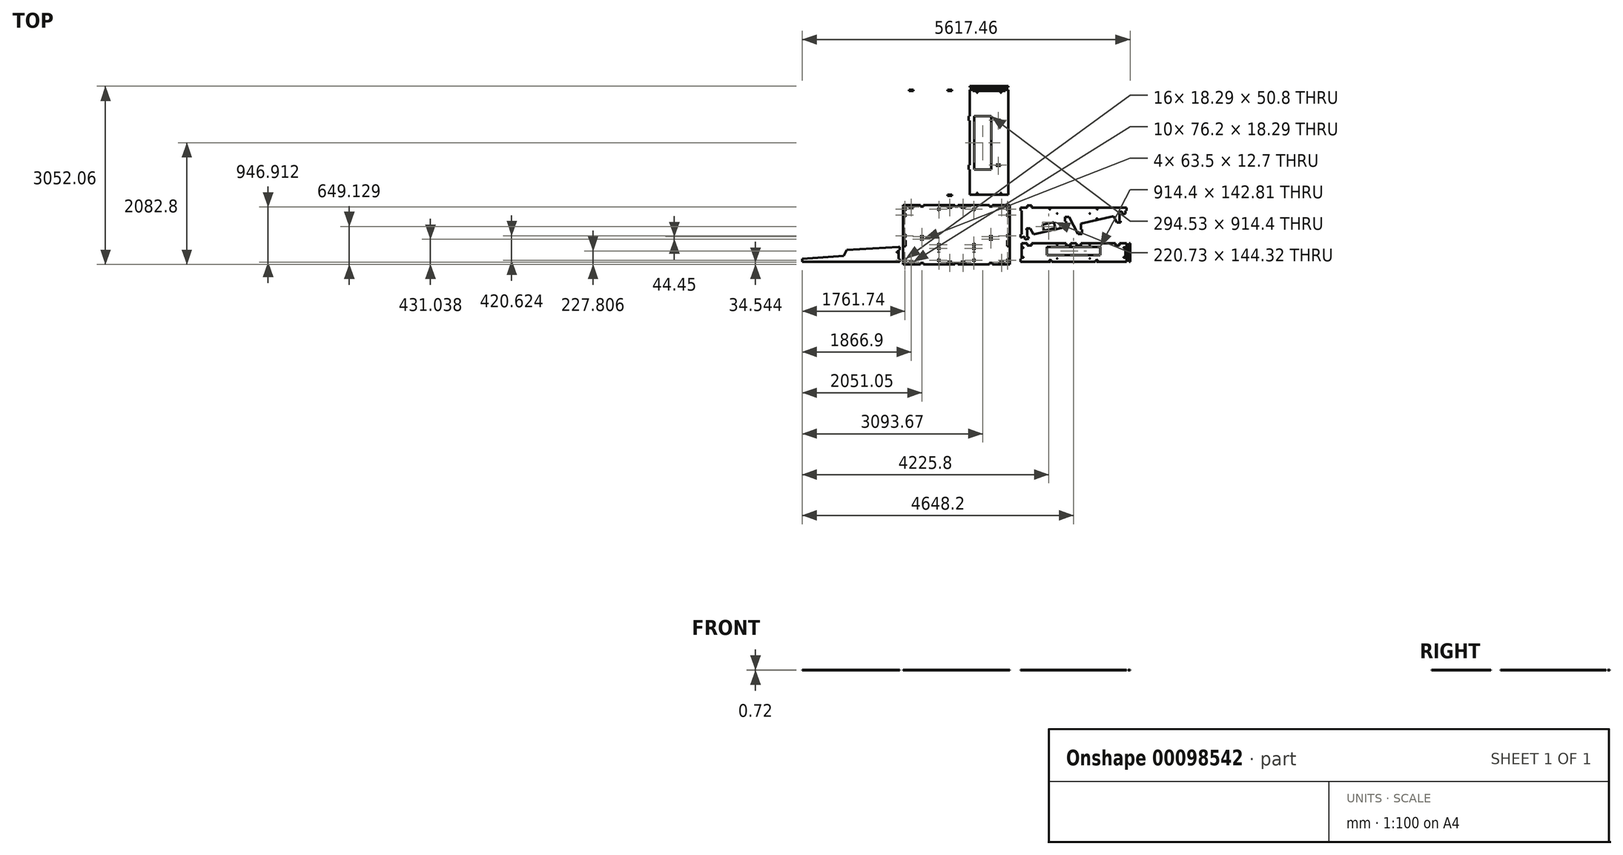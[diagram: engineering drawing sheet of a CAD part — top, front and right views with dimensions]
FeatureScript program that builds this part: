
annotation { "Feature Type Name" : "Feature", "Feature Type Description" : "" }
export const myFeature = defineFeature(function(context is Context, id is Id, definition is map)
    precondition{}
    {
        {
            assignVariable(context, id + "F0", {"name" : "ply34", "anyValue" : .72});
        }
        {
            var Q0;
            Q0=qCreatedBy(makeId("Top.planeOp"),FACE);
            var sketch = newSketch(context, id + "F1", { "sketchPlane" : qUnion([Q0])});
            skLineSegment(sketch, "E0.bottom", {"start": v(914.4, 508) * mm, "end": v(-914.4, 508) * mm});
            skLineSegment(sketch, "E0.top", {"start": v(914.4, -508) * mm, "end": v(-914.4, -508) * mm});
            skLineSegment(sketch, "E0.left", {"start": v(914.4, 508) * mm, "end": v(914.4, -508) * mm});
            skLineSegment(sketch, "E0.right", {"start": v(-914.4, 508) * mm, "end": v(-914.4, -508) * mm});
            skPoint(sketch, "E0.middle", {"position": v(0, 0) * mm});
            skLineSegment(sketch, "E1.bottom", {"start": v(889, 482.6) * mm, "end": v(-889, 482.6) * mm, "construction": true});
            skLineSegment(sketch, "E1.top", {"start": v(889, -482.6) * mm, "end": v(-889, -482.6) * mm, "construction": true});
            skLineSegment(sketch, "E1.left", {"start": v(889, 482.6) * mm, "end": v(889, -482.6) * mm, "construction": true});
            skLineSegment(sketch, "E1.right", {"start": v(-889, 482.6) * mm, "end": v(-889, -482.6) * mm, "construction": true});
            skLineSegment(sketch, "E2", {"start": v(0, 482.6) * mm, "end": v(0, -482.6) * mm, "construction": true});
            skLineSegment(sketch, "E3", {"start": v(0, 0) * mm, "end": v(-889, 0) * mm, "construction": true});
            skLineSegment(sketch, "E4", {"start": v(-444.5, 482.6) * mm, "end": v(-444.5, -482.6) * mm, "construction": true});
            skPoint(sketch, "E4.startSnap0", {"position": v(-444.5, 0) * mm});
            skLineSegment(sketch, "E5.bottom", {"start": v(-812.8, 482.6) * mm, "end": v(-736.6, 482.6) * mm});
            skLineSegment(sketch, "E5.top", {"start": v(-812.8, 464.31) * mm, "end": v(-736.6, 464.31) * mm});
            skLineSegment(sketch, "E5.left", {"start": v(-812.8, 482.6) * mm, "end": v(-812.8, 464.31) * mm});
            skLineSegment(sketch, "E5.right", {"start": v(-736.6, 482.6) * mm, "end": v(-736.6, 464.31) * mm});
            skLineSegment(sketch, "E6.MirrorCS", {"start": v(-76.2, 482.6) * mm, "end": v(-152.4, 482.6) * mm});
            skLineSegment(sketch, "E7.MirrorCS", {"start": v(-76.2, 464.31) * mm, "end": v(-152.4, 464.31) * mm});
            skLineSegment(sketch, "E8.MirrorCS", {"start": v(-152.4, 482.6) * mm, "end": v(-152.4, 464.31) * mm});
            skLineSegment(sketch, "E9.MirrorCS", {"start": v(-76.2, 482.6) * mm, "end": v(-76.2, 464.31) * mm});
            skLineSegment(sketch, "E10.MirrorCS", {"start": v(76.2, 482.6) * mm, "end": v(76.2, 464.31) * mm});
            skLineSegment(sketch, "E11.MirrorCS", {"start": v(736.6, 482.6) * mm, "end": v(736.6, 464.31) * mm});
            skLineSegment(sketch, "E12.MirrorCS", {"start": v(152.4, 482.6) * mm, "end": v(152.4, 464.31) * mm});
            skLineSegment(sketch, "E13.MirrorCS", {"start": v(812.8, 482.6) * mm, "end": v(812.8, 464.31) * mm});
            skLineSegment(sketch, "E14.MirrorCS", {"start": v(812.8, 482.6) * mm, "end": v(736.6, 482.6) * mm});
            skLineSegment(sketch, "E15.MirrorCS", {"start": v(76.2, 482.6) * mm, "end": v(152.4, 482.6) * mm});
            skLineSegment(sketch, "E16.MirrorCS", {"start": v(812.8, 464.31) * mm, "end": v(736.6, 464.31) * mm});
            skLineSegment(sketch, "E17.MirrorCS", {"start": v(76.2, 464.31) * mm, "end": v(152.4, 464.31) * mm});
            skLineSegment(sketch, "E18.MirrorCS", {"start": v(812.8, -482.6) * mm, "end": v(812.8, -464.31) * mm});
            skLineSegment(sketch, "E19.MirrorCS", {"start": v(-76.2, -482.6) * mm, "end": v(-76.2, -464.31) * mm});
            skLineSegment(sketch, "E20.MirrorCS", {"start": v(736.6, -482.6) * mm, "end": v(736.6, -464.31) * mm});
            skLineSegment(sketch, "E21.MirrorCS", {"start": v(-152.4, -482.6) * mm, "end": v(-152.4, -464.31) * mm});
            skLineSegment(sketch, "E22.MirrorCS", {"start": v(152.4, -482.6) * mm, "end": v(152.4, -464.31) * mm});
            skLineSegment(sketch, "E23.MirrorCS", {"start": v(-812.8, -482.6) * mm, "end": v(-812.8, -464.31) * mm});
            skLineSegment(sketch, "E24.MirrorCS", {"start": v(76.2, -482.6) * mm, "end": v(76.2, -464.31) * mm});
            skLineSegment(sketch, "E25.MirrorCS", {"start": v(-736.6, -482.6) * mm, "end": v(-736.6, -464.31) * mm});
            skLineSegment(sketch, "E26.MirrorCS", {"start": v(76.2, -482.6) * mm, "end": v(152.4, -482.6) * mm});
            skLineSegment(sketch, "E27.MirrorCS", {"start": v(812.8, -464.31) * mm, "end": v(736.6, -464.31) * mm});
            skLineSegment(sketch, "E28.MirrorCS", {"start": v(812.8, -482.6) * mm, "end": v(736.6, -482.6) * mm});
            skLineSegment(sketch, "E29.MirrorCS", {"start": v(-76.2, -464.31) * mm, "end": v(-152.4, -464.31) * mm});
            skLineSegment(sketch, "E30.MirrorCS", {"start": v(-76.2, -482.6) * mm, "end": v(-152.4, -482.6) * mm});
            skLineSegment(sketch, "E31.MirrorCS", {"start": v(76.2, -464.31) * mm, "end": v(152.4, -464.31) * mm});
            skLineSegment(sketch, "E32.MirrorCS", {"start": v(-812.8, -464.31) * mm, "end": v(-736.6, -464.31) * mm});
            skLineSegment(sketch, "E33.MirrorCS", {"start": v(-812.8, -482.6) * mm, "end": v(-736.6, -482.6) * mm});
            skLineSegment(sketch, "E34.bottom", {"start": v(292.1, 464.31) * mm, "end": v(310.39, 464.31) * mm});
            skLineSegment(sketch, "E34.top", {"start": v(292.1, 413.51) * mm, "end": v(310.39, 413.51) * mm});
            skLineSegment(sketch, "E34.left", {"start": v(292.1, 464.31) * mm, "end": v(292.1, 413.51) * mm});
            skLineSegment(sketch, "E34.right", {"start": v(310.39, 464.31) * mm, "end": v(310.39, 413.51) * mm});
            skLineSegment(sketch, "E35.bottom", {"start": v(292.1, -145.29) * mm, "end": v(310.39, -145.29) * mm});
            skLineSegment(sketch, "E35.top", {"start": v(292.1, -196.09) * mm, "end": v(310.39, -196.09) * mm});
            skLineSegment(sketch, "E35.left", {"start": v(292.1, -145.29) * mm, "end": v(292.1, -196.09) * mm});
            skLineSegment(sketch, "E35.right", {"start": v(310.39, -145.29) * mm, "end": v(310.39, -196.09) * mm});
            skLineSegment(sketch, "E36.MirrorCS", {"start": v(-292.1, -196.09) * mm, "end": v(-310.39, -196.09) * mm});
            skLineSegment(sketch, "E37.MirrorCS", {"start": v(-292.1, -145.29) * mm, "end": v(-310.39, -145.29) * mm});
            skLineSegment(sketch, "E38.MirrorCS", {"start": v(-292.1, 413.51) * mm, "end": v(-310.39, 413.51) * mm});
            skLineSegment(sketch, "E39.MirrorCS", {"start": v(-292.1, 464.31) * mm, "end": v(-310.39, 464.31) * mm});
            skLineSegment(sketch, "E40.MirrorCS", {"start": v(-292.1, -145.29) * mm, "end": v(-292.1, -196.09) * mm});
            skLineSegment(sketch, "E41.MirrorCS", {"start": v(-310.39, 464.31) * mm, "end": v(-310.39, 413.51) * mm});
            skLineSegment(sketch, "E42.MirrorCS", {"start": v(-310.39, -145.29) * mm, "end": v(-310.39, -196.09) * mm});
            skLineSegment(sketch, "E43.MirrorCS", {"start": v(-292.1, 464.31) * mm, "end": v(-292.1, 413.51) * mm});
            skLineSegment(sketch, "E44.bottom", {"start": v(-889, 685.8) * mm, "end": v(0, 685.8) * mm});
            skLineSegment(sketch, "E44.top", {"start": v(-889, 2463.8) * mm, "end": v(0, 2463.8) * mm});
            skLineSegment(sketch, "E44.left", {"start": v(-889, 685.8) * mm, "end": v(-889, 2463.8) * mm});
            skLineSegment(sketch, "E44.right", {"start": v(0, 685.8) * mm, "end": v(0, 2463.8) * mm});
            skLineSegment(sketch, "E45.bottom", {"start": v(-812.8, 685.8) * mm, "end": v(-736.6, 685.8) * mm});
            skLineSegment(sketch, "E45.top", {"start": v(-812.8, 667.51) * mm, "end": v(-736.6, 667.51) * mm});
            skLineSegment(sketch, "E45.left", {"start": v(-812.8, 685.8) * mm, "end": v(-812.8, 667.51) * mm});
            skLineSegment(sketch, "E45.right", {"start": v(-736.6, 685.8) * mm, "end": v(-736.6, 667.51) * mm});
            skLineSegment(sketch, "E46", {"start": v(-444.5, 685.8) * mm, "end": v(-444.5, 2463.8) * mm, "construction": true});
            skLineSegment(sketch, "E47", {"start": v(0, 1574.8) * mm, "end": v(-889, 1574.8) * mm, "construction": true});
            skLineSegment(sketch, "E48.MirrorCS", {"start": v(-76.2, 667.51) * mm, "end": v(-152.4, 667.51) * mm});
            skLineSegment(sketch, "E49.MirrorCS", {"start": v(-76.2, 685.8) * mm, "end": v(-152.4, 685.8) * mm});
            skLineSegment(sketch, "E50.MirrorCS", {"start": v(-152.4, 685.8) * mm, "end": v(-152.4, 667.51) * mm});
            skLineSegment(sketch, "E51.MirrorCS", {"start": v(-76.2, 685.8) * mm, "end": v(-76.2, 667.51) * mm});
            skLineSegment(sketch, "E52.MirrorCS", {"start": v(-812.8, 2482.09) * mm, "end": v(-736.6, 2482.09) * mm});
            skLineSegment(sketch, "E53.MirrorCS", {"start": v(-812.8, 2463.8) * mm, "end": v(-736.6, 2463.8) * mm});
            skLineSegment(sketch, "E54.MirrorCS", {"start": v(-812.8, 2463.8) * mm, "end": v(-812.8, 2482.09) * mm});
            skLineSegment(sketch, "E55.MirrorCS", {"start": v(-736.6, 2463.8) * mm, "end": v(-736.6, 2482.09) * mm});
            skLineSegment(sketch, "E56.MirrorCS", {"start": v(-152.4, 2463.8) * mm, "end": v(-152.4, 2482.09) * mm});
            skLineSegment(sketch, "E57.MirrorCS", {"start": v(-76.2, 2463.8) * mm, "end": v(-76.2, 2482.09) * mm});
            skLineSegment(sketch, "E58.MirrorCS", {"start": v(-76.2, 2482.09) * mm, "end": v(-152.4, 2482.09) * mm});
            skLineSegment(sketch, "E59.MirrorCS", {"start": v(-76.2, 2463.8) * mm, "end": v(-152.4, 2463.8) * mm});
            skLineSegment(sketch, "E60.0", {"start": v(870.71, 464.31) * mm, "end": v(-870.71, 464.31) * mm, "construction": true});
            skLineSegment(sketch, "E60.1", {"start": v(870.71, 464.31) * mm, "end": v(870.71, -464.31) * mm, "construction": true});
            skLineSegment(sketch, "E60.2", {"start": v(870.71, -464.31) * mm, "end": v(-870.71, -464.31) * mm, "construction": true});
            skLineSegment(sketch, "E60.3", {"start": v(-870.71, 464.31) * mm, "end": v(-870.71, -464.31) * mm, "construction": true});
            skLineSegment(sketch, "E61.bottom", {"start": v(-310.39, 464.31) * mm, "end": v(-292.1, 464.31) * mm, "construction": true});
            skLineSegment(sketch, "E61.top", {"start": v(-310.39, -196.09) * mm, "end": v(-292.1, -196.09) * mm, "construction": true});
            skLineSegment(sketch, "E61.left", {"start": v(-310.39, 464.31) * mm, "end": v(-310.39, -196.09) * mm, "construction": true});
            skLineSegment(sketch, "E61.right", {"start": v(-292.1, 464.31) * mm, "end": v(-292.1, -196.09) * mm, "construction": true});
            skLineSegment(sketch, "E62.bottom", {"start": v(292.1, 464.31) * mm, "end": v(310.39, 464.31) * mm, "construction": true});
            skLineSegment(sketch, "E62.top", {"start": v(292.1, -196.09) * mm, "end": v(310.39, -196.09) * mm, "construction": true});
            skLineSegment(sketch, "E62.left", {"start": v(292.1, 464.31) * mm, "end": v(292.1, -196.09) * mm, "construction": true});
            skLineSegment(sketch, "E62.right", {"start": v(310.39, 464.31) * mm, "end": v(310.39, -196.09) * mm, "construction": true});
            skLineSegment(sketch, "E63.bottom", {"start": v(228.6, 685.8) * mm, "end": v(889, 685.8) * mm});
            skLineSegment(sketch, "E63.top", {"start": v(228.6, 2463.8) * mm, "end": v(889, 2463.8) * mm});
            skLineSegment(sketch, "E63.left", {"start": v(228.6, 685.8) * mm, "end": v(228.6, 2463.8) * mm});
            skLineSegment(sketch, "E63.right", {"start": v(889, 685.8) * mm, "end": v(889, 2463.8) * mm});
            skLineSegment(sketch, "E64.bottom", {"start": v(228.6, 685.8) * mm, "end": v(279.4, 685.8) * mm});
            skLineSegment(sketch, "E64.top", {"start": v(228.6, 667.51) * mm, "end": v(279.4, 667.51) * mm});
            skLineSegment(sketch, "E64.left", {"start": v(228.6, 685.8) * mm, "end": v(228.6, 667.51) * mm});
            skLineSegment(sketch, "E64.right", {"start": v(279.4, 685.8) * mm, "end": v(279.4, 667.51) * mm});
            skLineSegment(sketch, "E65", {"start": v(558.8, 685.8) * mm, "end": v(558.8, 2463.8) * mm, "construction": true});
            skLineSegment(sketch, "E66", {"start": v(889, 1574.8) * mm, "end": v(228.6, 1574.8) * mm, "construction": true});
            skLineSegment(sketch, "E67.MirrorCS", {"start": v(889, 685.8) * mm, "end": v(838.2, 685.8) * mm});
            skLineSegment(sketch, "E68.MirrorCS", {"start": v(838.2, 685.8) * mm, "end": v(838.2, 667.51) * mm});
            skLineSegment(sketch, "E69.MirrorCS", {"start": v(889, 667.51) * mm, "end": v(838.2, 667.51) * mm});
            skLineSegment(sketch, "E70.MirrorCS", {"start": v(889, 685.8) * mm, "end": v(889, 667.51) * mm});
            skLineSegment(sketch, "E71.MirrorCS", {"start": v(889, 2463.8) * mm, "end": v(889, 2482.09) * mm});
            skLineSegment(sketch, "E72.MirrorCS", {"start": v(889, 2482.09) * mm, "end": v(838.2, 2482.09) * mm});
            skLineSegment(sketch, "E73.MirrorCS", {"start": v(838.2, 2463.8) * mm, "end": v(838.2, 2482.09) * mm});
            skLineSegment(sketch, "E74.MirrorCS", {"start": v(889, 2463.8) * mm, "end": v(838.2, 2463.8) * mm});
            skLineSegment(sketch, "E75.MirrorCS", {"start": v(228.6, 2463.8) * mm, "end": v(228.6, 2482.09) * mm});
            skLineSegment(sketch, "E76.MirrorCS", {"start": v(228.6, 2463.8) * mm, "end": v(279.4, 2463.8) * mm});
            skLineSegment(sketch, "E77.MirrorCS", {"start": v(279.4, 2463.8) * mm, "end": v(279.4, 2482.09) * mm});
            skLineSegment(sketch, "E78.MirrorCS", {"start": v(228.6, 2482.09) * mm, "end": v(279.4, 2482.09) * mm});
            skPoint(sketch, "E79.middle", {"position": v(558.8, 1574.8) * mm});
            skLineSegment(sketch, "E80.bottom", {"start": v(304.8, 2032) * mm, "end": v(599.33, 2032) * mm});
            skLineSegment(sketch, "E80.top", {"start": v(304.8, 1117.6) * mm, "end": v(599.33, 1117.6) * mm});
            skLineSegment(sketch, "E80.left", {"start": v(304.8, 2032) * mm, "end": v(304.8, 1117.6) * mm});
            skLineSegment(sketch, "E80.right", {"start": v(599.33, 2032) * mm, "end": v(599.33, 1117.6) * mm});
            skLineSegment(sketch, "E81", {"start": v(304.8, 1574.8) * mm, "end": v(599.33, 1574.8) * mm});
            skLineSegment(sketch, "E82.bottom", {"start": v(1117.6, 464.31) * mm, "end": v(2895.6, 464.31) * mm, "construction": true});
            skLineSegment(sketch, "E82.top", {"start": v(1117.6, -145.29) * mm, "end": v(2895.6, -145.29) * mm, "construction": true});
            skLineSegment(sketch, "E82.left", {"start": v(1117.6, 464.31) * mm, "end": v(1117.6, -145.29) * mm, "construction": true});
            skLineSegment(sketch, "E82.right", {"start": v(2895.6, 464.31) * mm, "end": v(2895.6, -145.29) * mm, "construction": true});
            skLineSegment(sketch, "E83", {"start": v(2133.6, 464.31) * mm, "end": v(2133.6, -145.29) * mm, "construction": true});
            skLineSegment(sketch, "E84", {"start": v(1117.6, -43.69) * mm, "end": v(2895.6, -43.69) * mm, "construction": true});
            skLineSegment(sketch, "E85", {"start": v(1117.6, 362.71) * mm, "end": v(2895.6, 362.71) * mm, "construction": true});
            skLineSegment(sketch, "E86", {"start": v(1117.6, 464.31) * mm, "end": v(2895.6, 464.31) * mm});
            skLineSegment(sketch, "E87", {"start": v(2895.6, 464.31) * mm, "end": v(2895.6, 362.71) * mm});
            skLineSegment(sketch, "E88", {"start": v(2895.6, 362.71) * mm, "end": v(1117.6, -43.69) * mm});
            skLineSegment(sketch, "E89", {"start": v(1117.6, -43.69) * mm, "end": v(1117.6, 464.31) * mm});
            skLineSegment(sketch, "E90", {"start": v(2133.6, 188.54) * mm, "end": v(2133.6, 14.22) * mm});
            skLineSegment(sketch, "E91", {"start": v(2133.6, 14.22) * mm, "end": v(2082.8, 14.22) * mm});
            skLineSegment(sketch, "E92", {"start": v(2082.8, 14.22) * mm, "end": v(2006.6, 159.51) * mm});
            skLineSegment(sketch, "E93.bottom", {"start": v(2133.6, 464.31) * mm, "end": v(2057.4, 464.31) * mm});
            skLineSegment(sketch, "E93.top", {"start": v(2133.6, 500.89) * mm, "end": v(2057.4, 500.89) * mm});
            skLineSegment(sketch, "E93.left", {"start": v(2133.6, 464.31) * mm, "end": v(2133.6, 500.89) * mm});
            skLineSegment(sketch, "E93.right", {"start": v(2057.4, 464.31) * mm, "end": v(2057.4, 500.89) * mm});
            skLineSegment(sketch, "E94.bottom", {"start": v(2133.6, 14.22) * mm, "end": v(2151.89, 14.22) * mm});
            skLineSegment(sketch, "E94.top", {"start": v(2133.6, 90.42) * mm, "end": v(2151.89, 90.42) * mm});
            skLineSegment(sketch, "E94.left", {"start": v(2133.6, 14.22) * mm, "end": v(2133.6, 90.42) * mm});
            skLineSegment(sketch, "E94.right", {"start": v(2151.89, 14.22) * mm, "end": v(2151.89, 90.42) * mm});
            skLineSegment(sketch, "E95", {"start": v(1879.6, 464.31) * mm, "end": v(1879.6, -145.29) * mm, "construction": true});
            skLineSegment(sketch, "E96.bottom", {"start": v(1879.6, 304.8) * mm, "end": v(1861.31, 304.8) * mm});
            skLineSegment(sketch, "E96.top", {"start": v(1879.6, 228.6) * mm, "end": v(1861.31, 228.6) * mm});
            skLineSegment(sketch, "E96.left", {"start": v(1879.6, 304.8) * mm, "end": v(1879.6, 228.6) * mm});
            skLineSegment(sketch, "E96.right", {"start": v(1861.31, 304.8) * mm, "end": v(1861.31, 228.6) * mm});
            skLineSegment(sketch, "E97", {"start": v(1879.6, 304.8) * mm, "end": v(1930.4, 304.8) * mm});
            skLineSegment(sketch, "E98", {"start": v(1879.6, 228.6) * mm, "end": v(1879.6, 130.48) * mm});
            skLineSegment(sketch, "E99.bottom", {"start": v(1879.6, -145.29) * mm, "end": v(1955.8, -145.29) * mm});
            skLineSegment(sketch, "E99.top", {"start": v(1879.6, -181.86) * mm, "end": v(1955.8, -181.86) * mm});
            skLineSegment(sketch, "E99.left", {"start": v(1879.6, -145.29) * mm, "end": v(1879.6, -181.86) * mm});
            skLineSegment(sketch, "E99.right", {"start": v(1955.8, -145.29) * mm, "end": v(1955.8, -181.86) * mm});
            skLineSegment(sketch, "E100", {"start": v(1117.6, -43.69) * mm, "end": v(1117.6, -145.29) * mm});
            skLineSegment(sketch, "E101", {"start": v(2895.6, -145.29) * mm, "end": v(1117.6, -145.29) * mm});
            skLineSegment(sketch, "E102", {"start": v(2895.6, -145.29) * mm, "end": v(2895.6, 362.71) * mm});
            skLineSegment(sketch, "E103", {"start": v(2006.6, 159.51) * mm, "end": v(1930.4, 304.8) * mm});
            skLineSegment(sketch, "E104.0", {"start": v(678.69, 2032) * mm, "end": v(678.69, 1117.6) * mm, "construction": true});
            skLineSegment(sketch, "E105.bottom", {"start": v(678.69, 1181.1) * mm, "end": v(754.89, 1181.1) * mm});
            skLineSegment(sketch, "E105.top", {"start": v(678.69, 1199.39) * mm, "end": v(754.89, 1199.39) * mm});
            skLineSegment(sketch, "E105.left", {"start": v(678.69, 1181.1) * mm, "end": v(678.69, 1199.39) * mm});
            skLineSegment(sketch, "E105.right", {"start": v(754.89, 1181.1) * mm, "end": v(754.89, 1199.39) * mm});
            skLineSegment(sketch, "E106.MirrorCS", {"start": v(754.89, 1968.5) * mm, "end": v(754.89, 1950.21) * mm});
            skLineSegment(sketch, "E107.MirrorCS", {"start": v(678.69, 1950.21) * mm, "end": v(754.89, 1950.21) * mm});
            skLineSegment(sketch, "E108.MirrorCS", {"start": v(678.69, 1968.5) * mm, "end": v(754.89, 1968.5) * mm});
            skLineSegment(sketch, "E109.MirrorCS", {"start": v(678.69, 1968.5) * mm, "end": v(678.69, 1950.21) * mm});
            skLineSegment(sketch, "E110.bottom", {"start": v(1117.6, 464.31) * mm, "end": v(1099.31, 464.31) * mm});
            skLineSegment(sketch, "E110.top", {"start": v(1117.6, 413.51) * mm, "end": v(1099.31, 413.51) * mm});
            skLineSegment(sketch, "E110.left", {"start": v(1117.6, 464.31) * mm, "end": v(1117.6, 413.51) * mm});
            skLineSegment(sketch, "E110.right", {"start": v(1099.31, 464.31) * mm, "end": v(1099.31, 413.51) * mm});
            skLineSegment(sketch, "E111.bottom", {"start": v(1117.6, -43.69) * mm, "end": v(1099.31, -43.69) * mm});
            skLineSegment(sketch, "E111.top", {"start": v(1117.6, 7.11) * mm, "end": v(1099.31, 7.11) * mm});
            skLineSegment(sketch, "E111.left", {"start": v(1117.6, -43.69) * mm, "end": v(1117.6, 7.11) * mm});
            skLineSegment(sketch, "E111.right", {"start": v(1099.31, -43.69) * mm, "end": v(1099.31, 7.11) * mm});
            skLineSegment(sketch, "E112.bottom", {"start": v(889, 464.31) * mm, "end": v(870.71, 464.31) * mm});
            skLineSegment(sketch, "E112.top", {"start": v(889, 413.51) * mm, "end": v(870.71, 413.51) * mm});
            skLineSegment(sketch, "E112.left", {"start": v(889, 464.31) * mm, "end": v(889, 413.51) * mm});
            skLineSegment(sketch, "E112.right", {"start": v(870.71, 464.31) * mm, "end": v(870.71, 413.51) * mm});
            skLineSegment(sketch, "E113.bottom", {"start": v(1099.31, -94.49) * mm, "end": v(1117.6, -94.49) * mm});
            skLineSegment(sketch, "E113.top", {"start": v(1099.31, -145.29) * mm, "end": v(1117.6, -145.29) * mm});
            skLineSegment(sketch, "E113.left", {"start": v(1099.31, -94.49) * mm, "end": v(1099.31, -145.29) * mm});
            skLineSegment(sketch, "E113.right", {"start": v(1117.6, -94.49) * mm, "end": v(1117.6, -145.29) * mm});
            skLineSegment(sketch, "E114.bottom", {"start": v(889, -94.49) * mm, "end": v(870.71, -94.49) * mm});
            skLineSegment(sketch, "E114.top", {"start": v(889, -145.29) * mm, "end": v(870.71, -145.29) * mm});
            skLineSegment(sketch, "E114.left", {"start": v(889, -94.49) * mm, "end": v(889, -145.29) * mm});
            skLineSegment(sketch, "E114.right", {"start": v(870.71, -94.49) * mm, "end": v(870.71, -145.29) * mm});
            skLineSegment(sketch, "E115.MirrorCS", {"start": v(-889, 464.31) * mm, "end": v(-870.71, 464.31) * mm});
            skLineSegment(sketch, "E116.MirrorCS", {"start": v(-889, -145.29) * mm, "end": v(-870.71, -145.29) * mm});
            skLineSegment(sketch, "E117.MirrorCS", {"start": v(-889, -94.49) * mm, "end": v(-870.71, -94.49) * mm});
            skLineSegment(sketch, "E118.MirrorCS", {"start": v(-889, 413.51) * mm, "end": v(-870.71, 413.51) * mm});
            skLineSegment(sketch, "E119.MirrorCS", {"start": v(-870.71, -94.49) * mm, "end": v(-870.71, -145.29) * mm});
            skLineSegment(sketch, "E120.MirrorCS", {"start": v(-889, -94.49) * mm, "end": v(-889, -145.29) * mm});
            skLineSegment(sketch, "E121.MirrorCS", {"start": v(-870.71, 464.31) * mm, "end": v(-870.71, 413.51) * mm});
            skLineSegment(sketch, "E122.MirrorCS", {"start": v(-889, 464.31) * mm, "end": v(-889, 413.51) * mm});
            skLineSegment(sketch, "E123", {"start": v(-50.8, 2463.8) * mm, "end": v(-50.8, 685.8) * mm, "construction": true});
            skLineSegment(sketch, "E124.bottom", {"start": v(889, 7.11) * mm, "end": v(870.71, 7.11) * mm});
            skLineSegment(sketch, "E124.top", {"start": v(889, -43.69) * mm, "end": v(870.71, -43.69) * mm});
            skLineSegment(sketch, "E124.left", {"start": v(889, 7.11) * mm, "end": v(889, -43.69) * mm});
            skLineSegment(sketch, "E124.right", {"start": v(870.71, 7.11) * mm, "end": v(870.71, -43.69) * mm});
            skLineSegment(sketch, "E125.MirrorCS", {"start": v(-870.71, 7.11) * mm, "end": v(-870.71, -43.69) * mm});
            skLineSegment(sketch, "E126.MirrorCS", {"start": v(-889, 7.11) * mm, "end": v(-889, -43.69) * mm});
            skLineSegment(sketch, "E127.MirrorCS", {"start": v(-889, -43.69) * mm, "end": v(-870.71, -43.69) * mm});
            skLineSegment(sketch, "E128.MirrorCS", {"start": v(-889, 7.11) * mm, "end": v(-870.71, 7.11) * mm});
            skLineSegment(sketch, "E129.MirrorCS", {"start": v(-838.2, 2463.8) * mm, "end": v(-838.2, 685.8) * mm, "construction": true});
            skLineSegment(sketch, "E130.0", {"start": v(1117.6, 482.6) * mm, "end": v(2895.6, 482.6) * mm, "construction": true});
            skLineSegment(sketch, "E131", {"start": v(1203.45, -24.06) * mm, "end": v(2936.75, 372.12) * mm, "construction": true});
            skLineSegment(sketch, "E132", {"start": v(2936.75, 372.12) * mm, "end": v(2940.82, 354.29) * mm, "construction": true});
            skLineSegment(sketch, "E133", {"start": v(2940.82, 354.29) * mm, "end": v(1207.53, -41.9) * mm, "construction": true});
            skLineSegment(sketch, "E134", {"start": v(1207.53, -41.9) * mm, "end": v(1203.45, -24.06) * mm, "construction": true});
            skLineSegment(sketch, "E135", {"start": v(2006.6, 159.51) * mm, "end": v(2133.6, 188.54) * mm, "construction": true});
            skPoint(sketch, "E136", {"position": v(2070.1, 174.03) * mm});
            skLineSegment(sketch, "E137.bottom", {"start": v(-50.8, 1676.4) * mm, "end": v(-69.09, 1676.4) * mm});
            skLineSegment(sketch, "E137.top", {"start": v(-50.8, 1473.2) * mm, "end": v(-69.09, 1473.2) * mm});
            skLineSegment(sketch, "E137.left", {"start": v(-50.8, 1676.4) * mm, "end": v(-50.8, 1473.2) * mm});
            skLineSegment(sketch, "E137.right", {"start": v(-69.09, 1676.4) * mm, "end": v(-69.09, 1473.2) * mm});
            skPoint(sketch, "E137.middle", {"position": v(-59.94, 1574.8) * mm});
            skLineSegment(sketch, "E138.bottom", {"start": v(-838.2, 685.8) * mm, "end": v(-819.91, 685.8) * mm});
            skLineSegment(sketch, "E138.top", {"start": v(-838.2, 698.5) * mm, "end": v(-819.91, 698.5) * mm});
            skLineSegment(sketch, "E138.left", {"start": v(-838.2, 685.8) * mm, "end": v(-838.2, 698.5) * mm});
            skLineSegment(sketch, "E138.right", {"start": v(-819.91, 685.8) * mm, "end": v(-819.91, 698.5) * mm});
            skLineSegment(sketch, "E139.MirrorCS", {"start": v(-69.09, 685.8) * mm, "end": v(-69.09, 698.5) * mm});
            skLineSegment(sketch, "E140.MirrorCS", {"start": v(-50.8, 685.8) * mm, "end": v(-50.8, 698.5) * mm});
            skLineSegment(sketch, "E141.MirrorCS", {"start": v(-50.8, 685.8) * mm, "end": v(-69.09, 685.8) * mm});
            skLineSegment(sketch, "E142.MirrorCS", {"start": v(-50.8, 698.5) * mm, "end": v(-69.09, 698.5) * mm});
            skLineSegment(sketch, "E143.MirrorCS", {"start": v(-69.09, 2463.8) * mm, "end": v(-69.09, 2451.1) * mm});
            skLineSegment(sketch, "E144.MirrorCS", {"start": v(-50.8, 2463.8) * mm, "end": v(-50.8, 2451.1) * mm});
            skLineSegment(sketch, "E145.MirrorCS", {"start": v(-50.8, 2463.8) * mm, "end": v(-69.09, 2463.8) * mm});
            skLineSegment(sketch, "E146.MirrorCS", {"start": v(-50.8, 2451.1) * mm, "end": v(-69.09, 2451.1) * mm});
            skLineSegment(sketch, "E147.MirrorCS", {"start": v(-838.2, 2463.8) * mm, "end": v(-819.91, 2463.8) * mm});
            skLineSegment(sketch, "E148.MirrorCS", {"start": v(-838.2, 2451.1) * mm, "end": v(-819.91, 2451.1) * mm});
            skLineSegment(sketch, "E149.MirrorCS", {"start": v(-819.91, 2463.8) * mm, "end": v(-819.91, 2451.1) * mm});
            skLineSegment(sketch, "E150.MirrorCS", {"start": v(-838.2, 2463.8) * mm, "end": v(-838.2, 2451.1) * mm});
            skLineSegment(sketch, "E151", {"start": v(1219.9, -39.06) * mm, "end": v(1215.83, -21.24) * mm});
            skLineSegment(sketch, "E152", {"start": v(1219.9, -39.06) * mm, "end": v(1232.29, -36.23) * mm});
            skLineSegment(sketch, "E153", {"start": v(1232.29, -36.23) * mm, "end": v(1239.36, -67.19) * mm});
            skLineSegment(sketch, "E154", {"start": v(1239.36, -67.19) * mm, "end": v(1177.46, -81.33) * mm});
            skLineSegment(sketch, "E155", {"start": v(1177.46, -81.33) * mm, "end": v(1166.3, -32.55) * mm});
            skLineSegment(sketch, "E156", {"start": v(1215.83, -21.24) * mm, "end": v(1215.83, 110.24) * mm});
            skLineSegment(sketch, "E157", {"start": v(1215.83, 110.24) * mm, "end": v(1266.63, 110.24) * mm});
            skLineSegment(sketch, "E158", {"start": v(1266.63, 110.24) * mm, "end": v(1322.77, 3.2) * mm});
            skLineSegment(sketch, "E159.bottom", {"start": v(1215.83, 110.24) * mm, "end": v(1197.54, 110.24) * mm});
            skLineSegment(sketch, "E159.top", {"start": v(1215.83, 84.84) * mm, "end": v(1197.54, 84.84) * mm});
            skLineSegment(sketch, "E159.left", {"start": v(1215.83, 110.24) * mm, "end": v(1215.83, 84.84) * mm});
            skLineSegment(sketch, "E159.right", {"start": v(1197.54, 110.24) * mm, "end": v(1197.54, 84.84) * mm});
            skLineSegment(sketch, "E160", {"start": v(2006.6, 159.51) * mm, "end": v(2059.14, -70.34) * mm, "construction": true});
            skLineSegment(sketch, "E161.MirrorCS", {"start": v(2801.44, 322.43) * mm, "end": v(2789.06, 319.6) * mm, "construction": true});
            skLineSegment(sketch, "E162.MirrorCS", {"start": v(2789.06, 319.6) * mm, "end": v(2796.14, 288.65) * mm, "construction": true});
            skLineSegment(sketch, "E163.MirrorCS", {"start": v(2813.82, 325.26) * mm, "end": v(2809.75, 343.09) * mm, "construction": true});
            skLineSegment(sketch, "E164.MirrorCS", {"start": v(2801.44, 322.43) * mm, "end": v(2797.37, 340.26) * mm, "construction": true});
            skLineSegment(sketch, "E165.MirrorCS", {"start": v(2740.25, 458.67) * mm, "end": v(2756.72, 466.62) * mm, "construction": true});
            skLineSegment(sketch, "E166.MirrorCS", {"start": v(2751.29, 435.8) * mm, "end": v(2767.76, 443.74) * mm, "construction": true});
            skLineSegment(sketch, "E167.MirrorCS", {"start": v(2796.14, 288.65) * mm, "end": v(2858.04, 302.8) * mm, "construction": true});
            skLineSegment(sketch, "E168.MirrorCS", {"start": v(2797.37, 340.26) * mm, "end": v(2740.25, 458.67) * mm, "construction": true});
            skLineSegment(sketch, "E169.MirrorCS", {"start": v(2858.04, 302.8) * mm, "end": v(2846.9, 351.58) * mm, "construction": true});
            skLineSegment(sketch, "E170.MirrorCS", {"start": v(2740.25, 458.67) * mm, "end": v(2694.5, 436.6) * mm, "construction": true});
            skLineSegment(sketch, "E171.MirrorCS", {"start": v(2694.5, 436.6) * mm, "end": v(2690.43, 315.82) * mm, "construction": true});
            skLineSegment(sketch, "E172.MirrorCS", {"start": v(2740.25, 458.67) * mm, "end": v(2751.29, 435.8) * mm, "construction": true});
            skLineSegment(sketch, "E173.MirrorCS", {"start": v(2756.72, 466.62) * mm, "end": v(2767.76, 443.74) * mm, "construction": true});
            skLineSegment(sketch, "E174.MirrorCS", {"start": v(2797.37, 234.19) * mm, "end": v(2815.66, 234.19) * mm});
            skLineSegment(sketch, "E175.MirrorCS", {"start": v(2793.3, 358.09) * mm, "end": v(2780.91, 355.26) * mm});
            skLineSegment(sketch, "E176.MirrorCS", {"start": v(2797.37, 208.79) * mm, "end": v(2815.66, 208.79) * mm});
            skLineSegment(sketch, "E177.MirrorCS", {"start": v(2793.3, 358.09) * mm, "end": v(2797.37, 340.26) * mm});
            skLineSegment(sketch, "E178.MirrorCS", {"start": v(2805.67, 360.92) * mm, "end": v(2809.75, 343.09) * mm, "construction": true});
            skLineSegment(sketch, "E179.MirrorCS", {"start": v(2797.37, 340.26) * mm, "end": v(2797.37, 208.79) * mm});
            skLineSegment(sketch, "E180.MirrorCS", {"start": v(2773.84, 386.2) * mm, "end": v(2835.74, 400.36) * mm});
            skLineSegment(sketch, "E181.MirrorCS", {"start": v(2780.91, 355.26) * mm, "end": v(2773.84, 386.2) * mm});
            skLineSegment(sketch, "E182.MirrorCS", {"start": v(2815.66, 208.79) * mm, "end": v(2815.66, 234.19) * mm});
            skLineSegment(sketch, "E183.MirrorCS", {"start": v(2797.37, 208.79) * mm, "end": v(2797.37, 234.19) * mm});
            skLineSegment(sketch, "E184.MirrorCS", {"start": v(2746.57, 208.79) * mm, "end": v(2690.43, 315.82) * mm});
            skLineSegment(sketch, "E185.MirrorCS", {"start": v(2797.37, 208.79) * mm, "end": v(2746.57, 208.79) * mm});
            skLineSegment(sketch, "E186.MirrorCS", {"start": v(2835.74, 400.36) * mm, "end": v(2846.9, 351.58) * mm});
            skLineSegment(sketch, "E187.bottom", {"start": v(1215.83, -145.29) * mm, "end": v(1292.03, -145.29) * mm});
            skLineSegment(sketch, "E187.top", {"start": v(1215.83, -181.86) * mm, "end": v(1292.03, -181.86) * mm});
            skLineSegment(sketch, "E187.left", {"start": v(1215.83, -145.29) * mm, "end": v(1215.83, -181.86) * mm});
            skLineSegment(sketch, "E187.right", {"start": v(1292.03, -145.29) * mm, "end": v(1292.03, -181.86) * mm});
            skLineSegment(sketch, "E188.bottom", {"start": v(2895.6, 464.31) * mm, "end": v(2913.89, 464.31) * mm});
            skLineSegment(sketch, "E188.top", {"start": v(2895.6, 413.51) * mm, "end": v(2913.89, 413.51) * mm});
            skLineSegment(sketch, "E188.left", {"start": v(2895.6, 464.31) * mm, "end": v(2895.6, 413.51) * mm});
            skLineSegment(sketch, "E188.right", {"start": v(2913.89, 464.31) * mm, "end": v(2913.89, 413.51) * mm});
            skLineSegment(sketch, "E189.bottom", {"start": v(2797.37, 464.31) * mm, "end": v(2721.17, 464.31) * mm});
            skLineSegment(sketch, "E189.top", {"start": v(2797.37, 500.89) * mm, "end": v(2721.17, 500.89) * mm});
            skLineSegment(sketch, "E189.left", {"start": v(2797.37, 464.31) * mm, "end": v(2797.37, 500.89) * mm});
            skLineSegment(sketch, "E189.right", {"start": v(2721.17, 464.31) * mm, "end": v(2721.17, 500.89) * mm});
            skLineSegment(sketch, "E190.bottom", {"start": v(2895.6, 362.71) * mm, "end": v(2913.89, 362.71) * mm});
            skLineSegment(sketch, "E190.top", {"start": v(2895.6, 311.91) * mm, "end": v(2913.89, 311.91) * mm});
            skLineSegment(sketch, "E190.left", {"start": v(2895.6, 362.71) * mm, "end": v(2895.6, 311.91) * mm});
            skLineSegment(sketch, "E190.right", {"start": v(2913.89, 362.71) * mm, "end": v(2913.89, 311.91) * mm});
            skLineSegment(sketch, "E191.bottom", {"start": v(2895.6, -145.29) * mm, "end": v(2913.89, -145.29) * mm});
            skLineSegment(sketch, "E191.top", {"start": v(2895.6, -94.49) * mm, "end": v(2913.89, -94.49) * mm});
            skLineSegment(sketch, "E191.left", {"start": v(2895.6, -145.29) * mm, "end": v(2895.6, -94.49) * mm});
            skLineSegment(sketch, "E191.right", {"start": v(2913.89, -145.29) * mm, "end": v(2913.89, -94.49) * mm});
            skLineSegment(sketch, "E192", {"start": v(2006.6, 159.51) * mm, "end": v(2006.6, -208.79) * mm, "construction": true});
            skPoint(sketch, "E192.endSnap0", {"position": v(2006.6, -145.29) * mm});
            skLineSegment(sketch, "E193.MirrorCS", {"start": v(2057.4, -145.29) * mm, "end": v(2057.4, -181.86) * mm});
            skLineSegment(sketch, "E194.MirrorCS", {"start": v(2133.6, -145.29) * mm, "end": v(2133.6, -181.86) * mm});
            skLineSegment(sketch, "E195.MirrorCS", {"start": v(2721.17, -145.29) * mm, "end": v(2721.17, -181.86) * mm});
            skLineSegment(sketch, "E196.MirrorCS", {"start": v(2797.37, -145.29) * mm, "end": v(2797.37, -181.86) * mm});
            skLineSegment(sketch, "E197.MirrorCS", {"start": v(2133.6, -181.86) * mm, "end": v(2057.4, -181.86) * mm});
            skLineSegment(sketch, "E198.MirrorCS", {"start": v(2133.6, -145.29) * mm, "end": v(2057.4, -145.29) * mm});
            skLineSegment(sketch, "E199.MirrorCS", {"start": v(2797.37, -181.86) * mm, "end": v(2721.17, -181.86) * mm});
            skLineSegment(sketch, "E200.MirrorCS", {"start": v(2797.37, -145.29) * mm, "end": v(2721.17, -145.29) * mm});
            skLineSegment(sketch, "E201", {"start": v(2690.43, 315.82) * mm, "end": v(2797.37, 340.26) * mm, "construction": true});
            skPoint(sketch, "E202", {"position": v(2743.9, 328.04) * mm});
            skLineSegment(sketch, "E203", {"start": v(-889, 2270.7) * mm, "end": v(0, 2270.7) * mm, "construction": true});
            skLineSegment(sketch, "E204.MirrorCS", {"start": v(1879.6, 464.31) * mm, "end": v(1955.8, 464.31) * mm});
            skLineSegment(sketch, "E205.MirrorCS", {"start": v(1879.6, 500.89) * mm, "end": v(1955.8, 500.89) * mm});
            skLineSegment(sketch, "E206.MirrorCS", {"start": v(1879.6, 464.31) * mm, "end": v(1879.6, 500.89) * mm});
            skLineSegment(sketch, "E207.MirrorCS", {"start": v(1955.8, 464.31) * mm, "end": v(1955.8, 500.89) * mm});
            skLineSegment(sketch, "E208.MirrorCS", {"start": v(1215.83, 500.89) * mm, "end": v(1292.03, 500.89) * mm});
            skLineSegment(sketch, "E209.MirrorCS", {"start": v(1215.83, 464.31) * mm, "end": v(1292.03, 464.31) * mm});
            skLineSegment(sketch, "E210.MirrorCS", {"start": v(1215.83, 464.31) * mm, "end": v(1215.83, 500.89) * mm});
            skLineSegment(sketch, "E211.MirrorCS", {"start": v(1292.03, 464.31) * mm, "end": v(1292.03, 500.89) * mm});
            skLineSegment(sketch, "E212.bottom", {"start": v(-50.8, 2359.6) * mm, "end": v(-69.09, 2359.6) * mm});
            skLineSegment(sketch, "E212.top", {"start": v(-50.8, 2181.8) * mm, "end": v(-69.09, 2181.8) * mm});
            skLineSegment(sketch, "E212.left", {"start": v(-50.8, 2359.6) * mm, "end": v(-50.8, 2181.8) * mm});
            skLineSegment(sketch, "E212.right", {"start": v(-69.09, 2359.6) * mm, "end": v(-69.09, 2181.8) * mm});
            skPoint(sketch, "E212.middle", {"position": v(-59.94, 2270.7) * mm});
            skLineSegment(sketch, "E213.MirrorCS", {"start": v(-838.2, 2181.8) * mm, "end": v(-819.91, 2181.8) * mm});
            skLineSegment(sketch, "E214.MirrorCS", {"start": v(-838.2, 2359.6) * mm, "end": v(-819.91, 2359.6) * mm});
            skLineSegment(sketch, "E215.MirrorCS", {"start": v(-819.91, 2359.6) * mm, "end": v(-819.91, 2181.8) * mm});
            skLineSegment(sketch, "E216.MirrorCS", {"start": v(-838.2, 2359.6) * mm, "end": v(-838.2, 2181.8) * mm});
            skPoint(sketch, "E217.MirrorP", {"position": v(-829.06, 2270.7) * mm});
            skLineSegment(sketch, "E218.MirrorCS", {"start": v(-50.8, 790) * mm, "end": v(-69.09, 790) * mm});
            skLineSegment(sketch, "E219.MirrorCS", {"start": v(-838.2, 967.8) * mm, "end": v(-819.91, 967.8) * mm});
            skLineSegment(sketch, "E220.MirrorCS", {"start": v(-838.2, 790) * mm, "end": v(-819.91, 790) * mm});
            skLineSegment(sketch, "E221.MirrorCS", {"start": v(-50.8, 967.8) * mm, "end": v(-69.09, 967.8) * mm});
            skLineSegment(sketch, "E222.MirrorCS", {"start": v(-50.8, 790) * mm, "end": v(-50.8, 967.8) * mm});
            skLineSegment(sketch, "E223.MirrorCS", {"start": v(-69.09, 790) * mm, "end": v(-69.09, 967.8) * mm});
            skLineSegment(sketch, "E224.MirrorCS", {"start": v(-819.91, 790) * mm, "end": v(-819.91, 967.8) * mm});
            skLineSegment(sketch, "E225.MirrorCS", {"start": v(-838.2, 790) * mm, "end": v(-838.2, 967.8) * mm});
            skPoint(sketch, "E226.MirrorP", {"position": v(-59.94, 878.9) * mm});
            skPoint(sketch, "E227.MirrorP", {"position": v(-829.06, 878.9) * mm});
            skLineSegment(sketch, "E228.MirrorCS", {"start": v(-838.2, 1473.2) * mm, "end": v(-819.91, 1473.2) * mm});
            skLineSegment(sketch, "E229.MirrorCS", {"start": v(-838.2, 1676.4) * mm, "end": v(-819.91, 1676.4) * mm});
            skPoint(sketch, "E230.MirrorP", {"position": v(-829.06, 1574.8) * mm});
            skLineSegment(sketch, "E231.MirrorCS", {"start": v(-819.91, 1676.4) * mm, "end": v(-819.91, 1473.2) * mm});
            skLineSegment(sketch, "E232.MirrorCS", {"start": v(-838.2, 1676.4) * mm, "end": v(-838.2, 1473.2) * mm});
            skPoint(sketch, "E233", {"position": v(2797.37, 482.6) * mm});
            skPoint(sketch, "E234", {"position": v(2797.37, 321.5) * mm});
            skLineSegment(sketch, "E235", {"start": v(1117.6, -145.29) * mm, "end": v(1117.6, -464.31) * mm});
            skLineSegment(sketch, "E236", {"start": v(1117.6, -464.31) * mm, "end": v(2895.6, -464.31) * mm});
            skLineSegment(sketch, "E237", {"start": v(2895.6, -464.31) * mm, "end": v(2895.6, -145.29) * mm});
            skLineSegment(sketch, "E238.bottom", {"start": v(1549.4, -351.6) * mm, "end": v(2463.8, -351.6) * mm});
            skLineSegment(sketch, "E238.top", {"start": v(1549.4, -208.79) * mm, "end": v(2463.8, -208.79) * mm});
            skLineSegment(sketch, "E238.left", {"start": v(1549.4, -351.6) * mm, "end": v(1549.4, -208.79) * mm});
            skLineSegment(sketch, "E238.right", {"start": v(2463.8, -351.6) * mm, "end": v(2463.8, -208.79) * mm});
            skLineSegment(sketch, "E239.0", {"start": v(2882.5, 378.48) * mm, "end": v(1114.88, -25.55) * mm, "construction": true});
            skLineSegment(sketch, "E240", {"start": v(1215.83, -73.88) * mm, "end": v(1117.6, -73.88) * mm, "construction": true});
            skLineSegment(sketch, "E241", {"start": v(1206.69, 110.24) * mm, "end": v(1206.69, -73.88) * mm, "construction": true});
            skLineSegment(sketch, "E242", {"start": v(716.79, 1199.39) * mm, "end": v(716.79, 1574.8) * mm, "construction": true});
            skLineSegment(sketch, "E243", {"start": v(-444.5, 1574.8) * mm, "end": v(-69.09, 1574.8) * mm, "construction": true});
            skLineSegment(sketch, "E244", {"start": v(2006.6, -407.96) * mm, "end": v(2382.01, -407.96) * mm, "construction": true});
            skLineSegment(sketch, "E245", {"start": v(2006.6, -351.6) * mm, "end": v(2006.6, -464.31) * mm, "construction": true});
            skLineSegment(sketch, "E246.bottom", {"start": v(2382.01, -464.31) * mm, "end": v(2400.3, -464.31) * mm});
            skLineSegment(sketch, "E246.top", {"start": v(2382.01, -438.91) * mm, "end": v(2400.3, -438.91) * mm});
            skLineSegment(sketch, "E246.left", {"start": v(2382.01, -464.31) * mm, "end": v(2382.01, -438.91) * mm});
            skLineSegment(sketch, "E246.right", {"start": v(2400.3, -464.31) * mm, "end": v(2400.3, -438.91) * mm});
            skPoint(sketch, "E247.endSnap0", {"position": v(2463.8, -280.2) * mm});
            skLineSegment(sketch, "E248", {"start": v(2391.16, -464.31) * mm, "end": v(2391.16, -280.2) * mm, "construction": true});
            skLineSegment(sketch, "E249.MirrorCS", {"start": v(1612.9, -464.31) * mm, "end": v(1612.9, -438.91) * mm});
            skLineSegment(sketch, "E250.MirrorCS", {"start": v(1631.19, -464.31) * mm, "end": v(1631.19, -438.91) * mm});
            skLineSegment(sketch, "E251.MirrorCS", {"start": v(1631.19, -464.31) * mm, "end": v(1612.9, -464.31) * mm});
            skLineSegment(sketch, "E252.MirrorCS", {"start": v(1631.19, -438.91) * mm, "end": v(1612.9, -438.91) * mm});
            skLineSegment(sketch, "E253.bottom", {"start": v(1117.6, -464.31) * mm, "end": v(1099.31, -464.31) * mm});
            skLineSegment(sketch, "E253.top", {"start": v(1117.6, -413.51) * mm, "end": v(1099.31, -413.51) * mm});
            skLineSegment(sketch, "E253.left", {"start": v(1117.6, -464.31) * mm, "end": v(1117.6, -413.51) * mm});
            skLineSegment(sketch, "E253.right", {"start": v(1099.31, -464.31) * mm, "end": v(1099.31, -413.51) * mm});
            skLineSegment(sketch, "E254.bottom", {"start": v(1117.6, -145.29) * mm, "end": v(1099.31, -145.29) * mm});
            skLineSegment(sketch, "E254.top", {"start": v(1117.6, -196.09) * mm, "end": v(1099.31, -196.09) * mm});
            skLineSegment(sketch, "E254.left", {"start": v(1117.6, -145.29) * mm, "end": v(1117.6, -196.09) * mm});
            skLineSegment(sketch, "E254.right", {"start": v(1099.31, -145.29) * mm, "end": v(1099.31, -196.09) * mm});
            skLineSegment(sketch, "E255.MirrorCS", {"start": v(2895.6, -464.31) * mm, "end": v(2913.89, -464.31) * mm});
            skLineSegment(sketch, "E256.MirrorCS", {"start": v(2895.6, -413.51) * mm, "end": v(2913.89, -413.51) * mm});
            skLineSegment(sketch, "E257.MirrorCS", {"start": v(2895.6, -464.31) * mm, "end": v(2895.6, -413.51) * mm});
            skLineSegment(sketch, "E258.MirrorCS", {"start": v(2913.89, -464.31) * mm, "end": v(2913.89, -413.51) * mm});
            skLineSegment(sketch, "E259.MirrorCS", {"start": v(2913.89, -145.29) * mm, "end": v(2913.89, -196.09) * mm});
            skLineSegment(sketch, "E260.MirrorCS", {"start": v(2895.6, -196.09) * mm, "end": v(2913.89, -196.09) * mm});
            skLineSegment(sketch, "E261.bottom", {"start": v(870.71, -464.31) * mm, "end": v(889, -464.31) * mm});
            skLineSegment(sketch, "E261.top", {"start": v(870.71, -413.51) * mm, "end": v(889, -413.51) * mm});
            skLineSegment(sketch, "E261.left", {"start": v(870.71, -464.31) * mm, "end": v(870.71, -413.51) * mm});
            skLineSegment(sketch, "E261.right", {"start": v(889, -464.31) * mm, "end": v(889, -413.51) * mm});
            skLineSegment(sketch, "E262.bottom", {"start": v(870.71, -145.29) * mm, "end": v(889, -145.29) * mm});
            skLineSegment(sketch, "E262.top", {"start": v(870.71, -196.09) * mm, "end": v(889, -196.09) * mm});
            skLineSegment(sketch, "E262.left", {"start": v(870.71, -145.29) * mm, "end": v(870.71, -196.09) * mm});
            skLineSegment(sketch, "E262.right", {"start": v(889, -145.29) * mm, "end": v(889, -196.09) * mm});
            skLineSegment(sketch, "E263.MirrorCS", {"start": v(-889, -145.29) * mm, "end": v(-889, -196.09) * mm});
            skLineSegment(sketch, "E264.MirrorCS", {"start": v(-870.71, -145.29) * mm, "end": v(-870.71, -196.09) * mm});
            skLineSegment(sketch, "E265.MirrorCS", {"start": v(-870.71, -196.09) * mm, "end": v(-889, -196.09) * mm});
            skLineSegment(sketch, "E266.MirrorCS", {"start": v(-870.71, -464.31) * mm, "end": v(-889, -464.31) * mm});
            skLineSegment(sketch, "E267.MirrorCS", {"start": v(-889, -464.31) * mm, "end": v(-889, -413.51) * mm});
            skLineSegment(sketch, "E268.MirrorCS", {"start": v(-870.71, -464.31) * mm, "end": v(-870.71, -413.51) * mm});
            skLineSegment(sketch, "E269.MirrorCS", {"start": v(-870.71, -413.51) * mm, "end": v(-889, -413.51) * mm});
            skLineSegment(sketch, "E270.bottom", {"start": v(-889, 879.28) * mm, "end": v(-870.71, 879.28) * mm});
            skLineSegment(sketch, "E270.top", {"start": v(-889, 764.98) * mm, "end": v(-870.71, 764.98) * mm});
            skLineSegment(sketch, "E270.left", {"start": v(-889, 879.28) * mm, "end": v(-889, 764.98) * mm});
            skLineSegment(sketch, "E270.right", {"start": v(-870.71, 879.28) * mm, "end": v(-870.71, 764.98) * mm});
            skPoint(sketch, "E270.middle", {"position": v(-879.86, 822.13) * mm});
            skLineSegment(sketch, "E271.bottom", {"start": v(-889, 1428.75) * mm, "end": v(-870.71, 1428.75) * mm});
            skLineSegment(sketch, "E271.top", {"start": v(-889, 1543.05) * mm, "end": v(-870.71, 1543.05) * mm});
            skLineSegment(sketch, "E271.left", {"start": v(-889, 1428.75) * mm, "end": v(-889, 1543.05) * mm});
            skLineSegment(sketch, "E271.right", {"start": v(-870.71, 1428.75) * mm, "end": v(-870.71, 1543.05) * mm});
            skPoint(sketch, "E271.middle", {"position": v(-879.86, 1485.9) * mm});
            skLineSegment(sketch, "E272", {"start": v(-879.86, 822.13) * mm, "end": v(-879.86, 685.8) * mm, "construction": true});
            skLineSegment(sketch, "E273", {"start": v(-879.86, 1485.9) * mm, "end": v(-879.86, 685.8) * mm, "construction": true});
            skLineSegment(sketch, "E274", {"start": v(1117.6, 500.89) * mm, "end": v(1253.93, 500.89) * mm, "construction": true});
            skLineSegment(sketch, "E275", {"start": v(1117.6, 500.89) * mm, "end": v(1917.7, 500.89) * mm, "construction": true});
            skLineSegment(sketch, "E276.MirrorCS", {"start": v(0, 879.28) * mm, "end": v(-18.29, 879.28) * mm});
            skLineSegment(sketch, "E277.MirrorCS", {"start": v(0, 879.28) * mm, "end": v(0, 764.98) * mm});
            skLineSegment(sketch, "E278.MirrorCS", {"start": v(-18.29, 1428.75) * mm, "end": v(-18.29, 1543.05) * mm});
            skPoint(sketch, "E279.MirrorP", {"position": v(-9.14, 1485.9) * mm});
            skLineSegment(sketch, "E280.MirrorCS", {"start": v(0, 1428.75) * mm, "end": v(0, 1543.05) * mm});
            skPoint(sketch, "E281.MirrorP", {"position": v(-9.14, 822.13) * mm});
            skLineSegment(sketch, "E282.MirrorCS", {"start": v(0, 1543.05) * mm, "end": v(-18.29, 1543.05) * mm});
            skLineSegment(sketch, "E283.MirrorCS", {"start": v(0, 764.98) * mm, "end": v(-18.29, 764.98) * mm});
            skLineSegment(sketch, "E284.MirrorCS", {"start": v(0, 1428.75) * mm, "end": v(-18.29, 1428.75) * mm});
            skLineSegment(sketch, "E285.MirrorCS", {"start": v(-18.29, 879.28) * mm, "end": v(-18.29, 764.98) * mm});
            skLineSegment(sketch, "E286.MirrorCS", {"start": v(-889, 2270.32) * mm, "end": v(-870.71, 2270.32) * mm});
            skLineSegment(sketch, "E287.MirrorCS", {"start": v(-889, 2384.62) * mm, "end": v(-870.71, 2384.62) * mm});
            skLineSegment(sketch, "E288.MirrorCS", {"start": v(-889, 2270.32) * mm, "end": v(-889, 2384.62) * mm});
            skLineSegment(sketch, "E289.MirrorCS", {"start": v(-870.71, 2270.32) * mm, "end": v(-870.71, 2384.62) * mm});
            skLineSegment(sketch, "E290.MirrorCS", {"start": v(-889, 1720.85) * mm, "end": v(-870.71, 1720.85) * mm});
            skLineSegment(sketch, "E291.MirrorCS", {"start": v(-889, 1606.55) * mm, "end": v(-870.71, 1606.55) * mm});
            skPoint(sketch, "E292.MirrorP", {"position": v(-879.86, 2327.47) * mm});
            skLineSegment(sketch, "E293.MirrorCS", {"start": v(-889, 1720.85) * mm, "end": v(-889, 1606.55) * mm});
            skPoint(sketch, "E294.MirrorP", {"position": v(-879.86, 1663.7) * mm});
            skLineSegment(sketch, "E295.MirrorCS", {"start": v(-870.71, 1720.85) * mm, "end": v(-870.71, 1606.55) * mm});
            skLineSegment(sketch, "E296.MirrorCS", {"start": v(0, 1720.85) * mm, "end": v(-18.29, 1720.85) * mm});
            skLineSegment(sketch, "E297.MirrorCS", {"start": v(0, 2384.62) * mm, "end": v(-18.29, 2384.62) * mm});
            skLineSegment(sketch, "E298.MirrorCS", {"start": v(0, 2270.32) * mm, "end": v(-18.29, 2270.32) * mm});
            skLineSegment(sketch, "E299.MirrorCS", {"start": v(0, 1606.55) * mm, "end": v(-18.29, 1606.55) * mm});
            skLineSegment(sketch, "E300.MirrorCS", {"start": v(0, 1720.85) * mm, "end": v(0, 1606.55) * mm});
            skLineSegment(sketch, "E301.MirrorCS", {"start": v(-18.29, 1720.85) * mm, "end": v(-18.29, 1606.55) * mm});
            skLineSegment(sketch, "E302.MirrorCS", {"start": v(-18.29, 2270.32) * mm, "end": v(-18.29, 2384.62) * mm});
            skLineSegment(sketch, "E303.MirrorCS", {"start": v(0, 2270.32) * mm, "end": v(0, 2384.62) * mm});
            skPoint(sketch, "E304.MirrorP", {"position": v(-9.14, 2327.47) * mm});
            skPoint(sketch, "E305.MirrorP", {"position": v(-9.14, 1663.7) * mm});
            skLineSegment(sketch, "E306.0", {"start": v(-889, 692.15) * mm, "end": v(0, 692.15) * mm, "construction": true});
            skLineSegment(sketch, "E307.bottom", {"start": v(228.6, 1117.6) * mm, "end": v(210.31, 1117.6) * mm});
            skLineSegment(sketch, "E307.top", {"start": v(228.6, 1193.8) * mm, "end": v(210.31, 1193.8) * mm});
            skLineSegment(sketch, "E307.left", {"start": v(228.6, 1117.6) * mm, "end": v(228.6, 1193.8) * mm});
            skLineSegment(sketch, "E307.right", {"start": v(210.31, 1117.6) * mm, "end": v(210.31, 1193.8) * mm});
            skPoint(sketch, "E307.middle", {"position": v(219.46, 1155.7) * mm});
            skLineSegment(sketch, "E308.MirrorCS", {"start": v(228.6, 1955.8) * mm, "end": v(210.31, 1955.8) * mm});
            skLineSegment(sketch, "E309.MirrorCS", {"start": v(228.6, 2032) * mm, "end": v(210.31, 2032) * mm});
            skLineSegment(sketch, "E310.MirrorCS", {"start": v(210.31, 2032) * mm, "end": v(210.31, 1955.8) * mm});
            skPoint(sketch, "E311.MirrorP", {"position": v(219.46, 1993.9) * mm});
            skLineSegment(sketch, "E312.MirrorCS", {"start": v(228.6, 2032) * mm, "end": v(228.6, 1955.8) * mm});
            skLineSegment(sketch, "E313.bottom", {"start": v(-292.1, 1098.55) * mm, "end": v(-310.39, 1098.55) * mm});
            skLineSegment(sketch, "E313.top", {"start": v(-292.1, 1212.85) * mm, "end": v(-310.39, 1212.85) * mm});
            skLineSegment(sketch, "E313.left", {"start": v(-292.1, 1098.55) * mm, "end": v(-292.1, 1212.85) * mm});
            skLineSegment(sketch, "E313.right", {"start": v(-310.39, 1098.55) * mm, "end": v(-310.39, 1212.85) * mm});
            skPoint(sketch, "E313.middle", {"position": v(-301.24, 1155.7) * mm});
            skPoint(sketch, "E313.middle.positionSnap0", {"position": v(-301.24, 464.31) * mm});
            skPoint(sketch, "E313.middle.positionSnap1", {"position": v(210.31, 1155.7) * mm});
            skPoint(sketch, "E313.centerSnap0", {"position": v(-301.24, 464.31) * mm});
            skPoint(sketch, "E313.centerSnap1", {"position": v(210.31, 1155.7) * mm});
            skLineSegment(sketch, "E314.MirrorCS", {"start": v(-596.9, 1212.85) * mm, "end": v(-578.61, 1212.85) * mm});
            skLineSegment(sketch, "E315.MirrorCS", {"start": v(-596.9, 1098.55) * mm, "end": v(-578.61, 1098.55) * mm});
            skLineSegment(sketch, "E316.MirrorCS", {"start": v(-596.9, 1098.55) * mm, "end": v(-596.9, 1212.85) * mm});
            skLineSegment(sketch, "E317.MirrorCS", {"start": v(-578.61, 1098.55) * mm, "end": v(-578.61, 1212.85) * mm});
            skPoint(sketch, "E318.MirrorP", {"position": v(-587.76, 1155.7) * mm});
            skLineSegment(sketch, "E319.MirrorCS", {"start": v(-292.1, 2051.05) * mm, "end": v(-310.39, 2051.05) * mm});
            skLineSegment(sketch, "E320.MirrorCS", {"start": v(-292.1, 1936.75) * mm, "end": v(-310.39, 1936.75) * mm});
            skLineSegment(sketch, "E321.MirrorCS", {"start": v(-596.9, 2051.05) * mm, "end": v(-578.61, 2051.05) * mm});
            skLineSegment(sketch, "E322.MirrorCS", {"start": v(-596.9, 1936.75) * mm, "end": v(-578.61, 1936.75) * mm});
            skLineSegment(sketch, "E323.MirrorCS", {"start": v(-292.1, 2051.05) * mm, "end": v(-292.1, 1936.75) * mm});
            skLineSegment(sketch, "E324.MirrorCS", {"start": v(-596.9, 2051.05) * mm, "end": v(-596.9, 1936.75) * mm});
            skLineSegment(sketch, "E325.MirrorCS", {"start": v(-578.61, 2051.05) * mm, "end": v(-578.61, 1936.75) * mm});
            skLineSegment(sketch, "E326.MirrorCS", {"start": v(-310.39, 2051.05) * mm, "end": v(-310.39, 1936.75) * mm});
            skPoint(sketch, "E327.MirrorP", {"position": v(-301.24, 1993.9) * mm});
            skPoint(sketch, "E328.MirrorP", {"position": v(-587.76, 1993.9) * mm});
            skLineSegment(sketch, "E329", {"start": v(1727.2, -464.31) * mm, "end": v(1727.2, 464.31) * mm, "construction": true});
            skCircle(sketch, "E330", {"center": v(1727.2, 362.71) * mm, "radius": 3.5 * mm});
            skCircle(sketch, "E331", {"center": v(1727.2, -43.69) * mm, "radius": 3.5 * mm});
            skLineSegment(sketch, "E332", {"start": v(1727.2, -145.29) * mm, "end": v(1727.2, -208.79) * mm, "construction": true});
            skCircle(sketch, "E333", {"center": v(1727.2, -177.04) * mm, "radius": 3.5 * mm});
            skLineSegment(sketch, "E334", {"start": v(1727.2, -464.31) * mm, "end": v(1727.2, -351.6) * mm, "construction": true});
            skCircle(sketch, "E335", {"center": v(1727.2, -407.96) * mm, "radius": 3.5 * mm});
            skCircle(sketch, "E336.MirrorC", {"center": v(2286, 362.71) * mm, "radius": 3.5 * mm});
            skCircle(sketch, "E337.MirrorC", {"center": v(2286, -43.69) * mm, "radius": 3.5 * mm});
            skCircle(sketch, "E338.MirrorC", {"center": v(2286, -177.04) * mm, "radius": 3.5 * mm});
            skCircle(sketch, "E339.MirrorC", {"center": v(2286, -407.96) * mm, "radius": 3.5 * mm});
            skLineSegment(sketch, "E340.bottom", {"start": v(2939.29, -196.09) * mm, "end": v(2957.58, -196.09) * mm});
            skLineSegment(sketch, "E340.top", {"start": v(2939.29, -413.51) * mm, "end": v(2957.58, -413.51) * mm});
            skLineSegment(sketch, "E340.left", {"start": v(2939.29, -196.09) * mm, "end": v(2939.29, -413.51) * mm});
            skLineSegment(sketch, "E340.right", {"start": v(2957.58, -196.09) * mm, "end": v(2957.58, -413.51) * mm});
            skLineSegment(sketch, "E341.bottom", {"start": v(2957.58, -464.31) * mm, "end": v(2975.86, -464.31) * mm});
            skLineSegment(sketch, "E341.top", {"start": v(2957.58, -145.29) * mm, "end": v(2975.86, -145.29) * mm});
            skLineSegment(sketch, "E341.left", {"start": v(2957.58, -464.31) * mm, "end": v(2957.58, -145.29) * mm});
            skLineSegment(sketch, "E341.right", {"start": v(2975.86, -464.31) * mm, "end": v(2975.86, -145.29) * mm});
            skLineSegment(sketch, "E342.bottom", {"start": v(279.4, 2507.49) * mm, "end": v(838.2, 2507.49) * mm});
            skLineSegment(sketch, "E342.top", {"start": v(279.4, 2525.78) * mm, "end": v(838.2, 2525.78) * mm});
            skLineSegment(sketch, "E342.left", {"start": v(279.4, 2507.49) * mm, "end": v(279.4, 2525.78) * mm});
            skLineSegment(sketch, "E342.right", {"start": v(838.2, 2507.49) * mm, "end": v(838.2, 2525.78) * mm});
            skLineSegment(sketch, "E343.bottom", {"start": v(889, 2525.78) * mm, "end": v(228.6, 2525.78) * mm});
            skLineSegment(sketch, "E343.top", {"start": v(889, 2544.06) * mm, "end": v(228.6, 2544.06) * mm});
            skLineSegment(sketch, "E343.left", {"start": v(889, 2525.78) * mm, "end": v(889, 2544.06) * mm});
            skLineSegment(sketch, "E343.right", {"start": v(228.6, 2525.78) * mm, "end": v(228.6, 2544.06) * mm});
            skLineSegment(sketch, "E344", {"start": v(-310.39, 134.11) * mm, "end": v(-870.71, 134.11) * mm, "construction": true});
            skLineSegment(sketch, "E345", {"start": v(-292.1, 134.11) * mm, "end": v(292.1, 134.11) * mm, "construction": true});
            skLineSegment(sketch, "E346.bottom", {"start": v(-615.95, 508) * mm, "end": v(-565.15, 508) * mm});
            skLineSegment(sketch, "E346.top", {"start": v(-615.95, 482.6) * mm, "end": v(-565.15, 482.6) * mm});
            skLineSegment(sketch, "E346.left", {"start": v(-615.95, 508) * mm, "end": v(-615.95, 482.6) * mm});
            skLineSegment(sketch, "E346.right", {"start": v(-565.15, 508) * mm, "end": v(-565.15, 482.6) * mm});
            skPoint(sketch, "E346.middle", {"position": v(-590.55, 495.3) * mm});
            skPoint(sketch, "E346.middle.positionSnap0", {"position": v(-590.55, 134.11) * mm});
            skPoint(sketch, "E346.centerSnap0", {"position": v(-590.55, 134.11) * mm});
            skLineSegment(sketch, "E347.bottom", {"start": v(-25.4, 508) * mm, "end": v(25.4, 508) * mm});
            skLineSegment(sketch, "E347.top", {"start": v(-25.4, 482.6) * mm, "end": v(25.4, 482.6) * mm});
            skLineSegment(sketch, "E347.left", {"start": v(-25.4, 508) * mm, "end": v(-25.4, 482.6) * mm});
            skLineSegment(sketch, "E347.right", {"start": v(25.4, 508) * mm, "end": v(25.4, 482.6) * mm});
            skPoint(sketch, "E347.middle", {"position": v(0, 495.3) * mm});
            skLineSegment(sketch, "E348.MirrorCS", {"start": v(565.15, 508) * mm, "end": v(565.15, 482.6) * mm});
            skLineSegment(sketch, "E349.MirrorCS", {"start": v(615.95, 508) * mm, "end": v(615.95, 482.6) * mm});
            skLineSegment(sketch, "E350.MirrorCS", {"start": v(615.95, 482.6) * mm, "end": v(565.15, 482.6) * mm});
            skLineSegment(sketch, "E351.MirrorCS", {"start": v(615.95, 508) * mm, "end": v(565.15, 508) * mm});
            skPoint(sketch, "E352.MirrorP", {"position": v(590.55, 495.3) * mm});
            skLineSegment(sketch, "E353.MirrorCS", {"start": v(-615.95, -508) * mm, "end": v(-565.15, -508) * mm});
            skLineSegment(sketch, "E354.MirrorCS", {"start": v(-615.95, -482.6) * mm, "end": v(-565.15, -482.6) * mm});
            skLineSegment(sketch, "E355.MirrorCS", {"start": v(-615.95, -508) * mm, "end": v(-615.95, -482.6) * mm});
            skLineSegment(sketch, "E356.MirrorCS", {"start": v(-565.15, -508) * mm, "end": v(-565.15, -482.6) * mm});
            skPoint(sketch, "E357.MirrorP", {"position": v(-590.55, -495.3) * mm});
            skLineSegment(sketch, "E358.MirrorCS", {"start": v(-25.4, -508) * mm, "end": v(25.4, -508) * mm});
            skLineSegment(sketch, "E359.MirrorCS", {"start": v(-25.4, -482.6) * mm, "end": v(25.4, -482.6) * mm});
            skLineSegment(sketch, "E360.MirrorCS", {"start": v(-25.4, -508) * mm, "end": v(-25.4, -482.6) * mm});
            skPoint(sketch, "E361.MirrorP", {"position": v(0, -495.3) * mm});
            skLineSegment(sketch, "E362.MirrorCS", {"start": v(25.4, -508) * mm, "end": v(25.4, -482.6) * mm});
            skLineSegment(sketch, "E363.MirrorCS", {"start": v(615.95, -508) * mm, "end": v(565.15, -508) * mm});
            skLineSegment(sketch, "E364.MirrorCS", {"start": v(615.95, -482.6) * mm, "end": v(565.15, -482.6) * mm});
            skPoint(sketch, "E365.MirrorP", {"position": v(590.55, -495.3) * mm});
            skLineSegment(sketch, "E366.MirrorCS", {"start": v(615.95, -508) * mm, "end": v(615.95, -482.6) * mm});
            skLineSegment(sketch, "E367.MirrorCS", {"start": v(565.15, -508) * mm, "end": v(565.15, -482.6) * mm});
            skLineSegment(sketch, "E368.bottom", {"start": v(889, 362.71) * mm, "end": v(870.71, 362.71) * mm});
            skLineSegment(sketch, "E368.top", {"start": v(889, 311.91) * mm, "end": v(870.71, 311.91) * mm});
            skLineSegment(sketch, "E368.left", {"start": v(889, 362.71) * mm, "end": v(889, 311.91) * mm});
            skLineSegment(sketch, "E368.right", {"start": v(870.71, 362.71) * mm, "end": v(870.71, 311.91) * mm});
            skLineSegment(sketch, "E369.MirrorCS", {"start": v(-870.71, 362.71) * mm, "end": v(-870.71, 311.91) * mm});
            skLineSegment(sketch, "E370.MirrorCS", {"start": v(-889, 362.71) * mm, "end": v(-889, 311.91) * mm});
            skLineSegment(sketch, "E371.MirrorCS", {"start": v(-889, 311.91) * mm, "end": v(-870.71, 311.91) * mm});
            skLineSegment(sketch, "E372.MirrorCS", {"start": v(-889, 362.71) * mm, "end": v(-870.71, 362.71) * mm});
            skLineSegment(sketch, "E373.bottom", {"start": v(-736.6, 685.8) * mm, "end": v(-152.4, 685.8) * mm});
            skLineSegment(sketch, "E373.top", {"start": v(-736.6, 736.6) * mm, "end": v(-152.4, 736.6) * mm});
            skLineSegment(sketch, "E373.left", {"start": v(-736.6, 685.8) * mm, "end": v(-736.6, 736.6) * mm});
            skLineSegment(sketch, "E373.right", {"start": v(-152.4, 685.8) * mm, "end": v(-152.4, 736.6) * mm});
            skLineSegment(sketch, "E374.MirrorCS", {"start": v(-736.6, 2463.8) * mm, "end": v(-736.6, 2413) * mm});
            skLineSegment(sketch, "E375.MirrorCS", {"start": v(-736.6, 2413) * mm, "end": v(-152.4, 2413) * mm});
            skLineSegment(sketch, "E376.MirrorCS", {"start": v(-152.4, 2463.8) * mm, "end": v(-152.4, 2413) * mm});
            skLineSegment(sketch, "E377", {"start": v(2133.6, 464.31) * mm, "end": v(2133.6, 169.78) * mm, "construction": true});
            skLineSegment(sketch, "E378", {"start": v(1215.83, -145.29) * mm, "end": v(1215.83, -2.48) * mm, "construction": true});
            skLineSegment(sketch, "E379.0", {"start": v(1694.57, 114.25) * mm, "end": v(1496.48, 68.97) * mm});
            skLineSegment(sketch, "E380", {"start": v(1601.18, 66.85) * mm, "end": v(1595.52, 91.6) * mm, "construction": true});
            skLineSegment(sketch, "E381", {"start": v(1322.77, 3.2) * mm, "end": v(1879.6, 130.48) * mm, "construction": true});
            skLineSegment(sketch, "E382", {"start": v(1496.48, 68.97) * mm, "end": v(1473.84, 168.01) * mm});
            skLineSegment(sketch, "E383", {"start": v(1473.84, 168.01) * mm, "end": v(1671.93, 213.3) * mm});
            skLineSegment(sketch, "E384", {"start": v(1671.93, 213.3) * mm, "end": v(1694.57, 114.25) * mm});
            skLineSegment(sketch, "E385", {"start": v(1601.18, 66.85) * mm, "end": v(1606.84, 42.08) * mm, "construction": true});
            skCircle(sketch, "E386", {"center": v(1606.84, 42.08) * mm, "radius": 5.59 * mm, "construction": true});
            skCircle(sketch, "E387.MirrorC", {"center": v(2417.68, 227.42) * mm, "radius": 5.59 * mm, "construction": true});
            skCircle(sketch, "E388.MirrorC", {"center": v(2406.36, 276.94) * mm, "radius": 5.59 * mm});
            skLineSegment(sketch, "E389", {"start": v(1600.2, 500.89) * mm, "end": v(1600.2, 438.91) * mm, "construction": true});
            skCircle(sketch, "E390", {"center": v(1600.2, 438.91) * mm, "radius": 5.59 * mm});
            skCircle(sketch, "E391.MirrorC", {"center": v(2413, 438.91) * mm, "radius": 5.59 * mm});
            skCircle(sketch, "E392", {"center": v(-9.14, 1168.4) * mm, "radius": 3.81 * mm});
            skPoint(sketch, "E392.centerSnap0", {"position": v(-9.14, 879.28) * mm});
            skCircle(sketch, "E393.MirrorC", {"center": v(-879.86, 1168.4) * mm, "radius": 3.81 * mm});
            skCircle(sketch, "E394.MirrorC", {"center": v(-879.86, 1981.2) * mm, "radius": 3.81 * mm});
            skCircle(sketch, "E395.MirrorC", {"center": v(-9.14, 1981.2) * mm, "radius": 3.81 * mm});
            skCircle(sketch, "E396", {"center": v(1917.7, 475.49) * mm, "radius": 5.59 * mm});
            skCircle(sketch, "E397.MirrorC", {"center": v(2095.5, 475.49) * mm, "radius": 5.59 * mm});
            skLineSegment(sketch, "E398", {"start": v(3102.86, 464.31) * mm, "end": v(3102.86, -464.31) * mm, "construction": true});
            skLineSegment(sketch, "E399", {"start": v(3102.86, 0) * mm, "end": v(2895.6, 0) * mm, "construction": true});
            skCircle(sketch, "E400.MirrorC", {"center": v(1600.2, -438.91) * mm, "radius": 5.59 * mm});
            skCircle(sketch, "E401.MirrorC", {"center": v(2413, -438.91) * mm, "radius": 5.59 * mm});
            skLineSegment(sketch, "E402", {"start": v(-444.5, 768.35) * mm, "end": v(-495.3, 768.35) * mm});
            skLineSegment(sketch, "E403", {"start": v(-444.5, 768.35) * mm, "end": v(-393.7, 768.35) * mm});
            skLineSegment(sketch, "E404.bottom", {"start": v(-495.3, 768.35) * mm, "end": v(-393.7, 768.35) * mm});
            skLineSegment(sketch, "E404.top", {"start": v(-495.3, 781.05) * mm, "end": v(-393.7, 781.05) * mm});
            skLineSegment(sketch, "E404.left", {"start": v(-495.3, 768.35) * mm, "end": v(-495.3, 781.05) * mm});
            skLineSegment(sketch, "E404.right", {"start": v(-393.7, 768.35) * mm, "end": v(-393.7, 781.05) * mm});
            skLineSegment(sketch, "E405.MirrorCS", {"start": v(-393.7, 2381.25) * mm, "end": v(-393.7, 2368.55) * mm});
            skLineSegment(sketch, "E406.MirrorCS", {"start": v(-495.3, 2381.25) * mm, "end": v(-495.3, 2368.55) * mm});
            skLineSegment(sketch, "E407.MirrorCS", {"start": v(-444.5, 2381.25) * mm, "end": v(-393.7, 2381.25) * mm});
            skLineSegment(sketch, "E408.MirrorCS", {"start": v(-444.5, 2381.25) * mm, "end": v(-495.3, 2381.25) * mm});
            skLineSegment(sketch, "E409.MirrorCS", {"start": v(-495.3, 2368.55) * mm, "end": v(-393.7, 2368.55) * mm});
            skLineSegment(sketch, "E410.MirrorCS", {"start": v(-495.3, 2381.25) * mm, "end": v(-393.7, 2381.25) * mm});
            skLineSegment(sketch, "E411", {"start": v(736.6, -464.31) * mm, "end": v(736.6, -83.31) * mm, "construction": true});
            skLineSegment(sketch, "E412.bottom", {"start": v(622.3, -83.31) * mm, "end": v(558.8, -83.31) * mm});
            skLineSegment(sketch, "E412.top", {"start": v(622.3, -70.61) * mm, "end": v(558.8, -70.61) * mm});
            skLineSegment(sketch, "E412.left", {"start": v(622.3, -83.31) * mm, "end": v(622.3, -70.61) * mm});
            skLineSegment(sketch, "E412.right", {"start": v(558.8, -83.31) * mm, "end": v(558.8, -70.61) * mm});
            skPoint(sketch, "E412.middle", {"position": v(590.55, -76.96) * mm});
            skLineSegment(sketch, "E413.bottom", {"start": v(622.3, -38.86) * mm, "end": v(558.8, -38.86) * mm});
            skLineSegment(sketch, "E413.top", {"start": v(622.3, -26.16) * mm, "end": v(558.8, -26.16) * mm});
            skLineSegment(sketch, "E413.left", {"start": v(622.3, -38.86) * mm, "end": v(622.3, -26.16) * mm});
            skLineSegment(sketch, "E413.right", {"start": v(558.8, -38.86) * mm, "end": v(558.8, -26.16) * mm});
            skPoint(sketch, "E413.middle", {"position": v(590.55, -32.51) * mm});
            skLineSegment(sketch, "E414.MirrorCS", {"start": v(-558.8, -38.86) * mm, "end": v(-558.8, -26.16) * mm});
            skLineSegment(sketch, "E415.MirrorCS", {"start": v(-622.3, -38.86) * mm, "end": v(-622.3, -26.16) * mm});
            skLineSegment(sketch, "E416.MirrorCS", {"start": v(-558.8, -83.31) * mm, "end": v(-558.8, -70.61) * mm});
            skLineSegment(sketch, "E417.MirrorCS", {"start": v(-622.3, -83.31) * mm, "end": v(-622.3, -70.61) * mm});
            skPoint(sketch, "E418.MirrorP", {"position": v(-590.55, -32.51) * mm});
            skLineSegment(sketch, "E419.MirrorCS", {"start": v(-622.3, -26.16) * mm, "end": v(-558.8, -26.16) * mm});
            skLineSegment(sketch, "E420.MirrorCS", {"start": v(-622.3, -38.86) * mm, "end": v(-558.8, -38.86) * mm});
            skPoint(sketch, "E421.MirrorP", {"position": v(-590.55, -76.96) * mm});
            skLineSegment(sketch, "E422.MirrorCS", {"start": v(-622.3, -83.31) * mm, "end": v(-558.8, -83.31) * mm});
            skLineSegment(sketch, "E423.MirrorCS", {"start": v(-622.3, -70.61) * mm, "end": v(-558.8, -70.61) * mm});
            skPoint(sketch, "E424.MirrorP", {"position": v(-301.24, -464.31) * mm});
            skLineSegment(sketch, "E425.MirrorCS", {"start": v(-310.39, -464.31) * mm, "end": v(-292.1, -464.31) * mm, "construction": true});
            skLineSegment(sketch, "E426.MirrorCS", {"start": v(-292.1, -464.31) * mm, "end": v(-292.1, -413.51) * mm});
            skLineSegment(sketch, "E427.MirrorCS", {"start": v(-310.39, -464.31) * mm, "end": v(-310.39, -413.51) * mm});
            skLineSegment(sketch, "E428.MirrorCS", {"start": v(-292.1, -464.31) * mm, "end": v(-310.39, -464.31) * mm});
            skLineSegment(sketch, "E429.MirrorCS", {"start": v(-292.1, -413.51) * mm, "end": v(-310.39, -413.51) * mm});
            skLineSegment(sketch, "E430.MirrorCS", {"start": v(292.1, -464.31) * mm, "end": v(310.39, -464.31) * mm, "construction": true});
            skLineSegment(sketch, "E431.MirrorCS", {"start": v(292.1, -464.31) * mm, "end": v(292.1, -413.51) * mm});
            skLineSegment(sketch, "E432.MirrorCS", {"start": v(310.39, -464.31) * mm, "end": v(310.39, -413.51) * mm});
            skLineSegment(sketch, "E433.MirrorCS", {"start": v(292.1, -464.31) * mm, "end": v(310.39, -464.31) * mm});
            skLineSegment(sketch, "E434.MirrorCS", {"start": v(292.1, -413.51) * mm, "end": v(310.39, -413.51) * mm});
            skLineSegment(sketch, "E435", {"start": v(0, -464.31) * mm, "end": v(0, -210.31) * mm, "construction": true});
            skLineSegment(sketch, "E436", {"start": v(0, -337.31) * mm, "end": v(-292.1, -337.31) * mm, "construction": true});
            skPoint(sketch, "E437.MirrorP", {"position": v(-301.24, -210.31) * mm});
            skLineSegment(sketch, "E438.MirrorCS", {"start": v(-310.39, -210.31) * mm, "end": v(-292.1, -210.31) * mm, "construction": true});
            skLineSegment(sketch, "E439.MirrorCS", {"start": v(-292.1, -261.11) * mm, "end": v(-310.39, -261.11) * mm});
            skLineSegment(sketch, "E440.MirrorCS", {"start": v(-292.1, -210.31) * mm, "end": v(-310.39, -210.31) * mm});
            skLineSegment(sketch, "E441.MirrorCS", {"start": v(-310.39, -210.31) * mm, "end": v(-310.39, -261.11) * mm});
            skLineSegment(sketch, "E442.MirrorCS", {"start": v(-292.1, -210.31) * mm, "end": v(-292.1, -261.11) * mm});
            skLineSegment(sketch, "E443.MirrorCS", {"start": v(310.39, -210.31) * mm, "end": v(292.1, -210.31) * mm, "construction": true});
            skPoint(sketch, "E444.MirrorP", {"position": v(301.24, -210.31) * mm});
            skLineSegment(sketch, "E445.MirrorCS", {"start": v(292.1, -210.31) * mm, "end": v(310.39, -210.31) * mm});
            skLineSegment(sketch, "E446.MirrorCS", {"start": v(310.39, -210.31) * mm, "end": v(310.39, -261.11) * mm});
            skLineSegment(sketch, "E447.MirrorCS", {"start": v(292.1, -210.31) * mm, "end": v(292.1, -261.11) * mm});
            skLineSegment(sketch, "E448.MirrorCS", {"start": v(292.1, -261.11) * mm, "end": v(310.39, -261.11) * mm});
            skLineSegment(sketch, "E449", {"start": v(-990.6, -210.31) * mm, "end": v(-990.6, -464.31) * mm});
            skLineSegment(sketch, "E450", {"start": v(-990.6, -464.31) * mm, "end": v(-2641.6, -464.31) * mm});
            skLineSegment(sketch, "E451", {"start": v(-2641.6, -464.31) * mm, "end": v(-2641.6, -413.51) * mm});
            skLineSegment(sketch, "E452", {"start": v(-2641.6, -413.51) * mm, "end": v(-1930.4, -362.71) * mm});
            skLineSegment(sketch, "E453.bottom", {"start": v(-990.6, -210.31) * mm, "end": v(-972.31, -210.31) * mm});
            skLineSegment(sketch, "E453.top", {"start": v(-990.6, -261.11) * mm, "end": v(-972.31, -261.11) * mm});
            skLineSegment(sketch, "E453.left", {"start": v(-990.6, -210.31) * mm, "end": v(-990.6, -261.11) * mm});
            skLineSegment(sketch, "E453.right", {"start": v(-972.31, -210.31) * mm, "end": v(-972.31, -261.11) * mm});
            skLineSegment(sketch, "E454.bottom", {"start": v(-990.6, -464.31) * mm, "end": v(-972.31, -464.31) * mm});
            skLineSegment(sketch, "E454.top", {"start": v(-990.6, -413.51) * mm, "end": v(-972.31, -413.51) * mm});
            skLineSegment(sketch, "E454.left", {"start": v(-990.6, -464.31) * mm, "end": v(-990.6, -413.51) * mm});
            skLineSegment(sketch, "E454.right", {"start": v(-972.31, -464.31) * mm, "end": v(-972.31, -413.51) * mm});
            skLineSegment(sketch, "E455.bottom", {"start": v(-1403.35, -464.31) * mm, "end": v(-1517.65, -464.31) * mm});
            skLineSegment(sketch, "E455.top", {"start": v(-1403.35, -482.6) * mm, "end": v(-1517.65, -482.6) * mm});
            skLineSegment(sketch, "E455.left", {"start": v(-1403.35, -464.31) * mm, "end": v(-1403.35, -482.6) * mm});
            skLineSegment(sketch, "E455.right", {"start": v(-1517.65, -464.31) * mm, "end": v(-1517.65, -482.6) * mm});
            skPoint(sketch, "E455.middle", {"position": v(-1460.5, -473.46) * mm});
            skLineSegment(sketch, "E456.0", {"start": v(-1879.6, -210.31) * mm, "end": v(-1879.6, -464.31) * mm, "construction": true});
            skLineSegment(sketch, "E457.MirrorCS", {"start": v(-2355.85, -464.31) * mm, "end": v(-2241.55, -464.31) * mm});
            skLineSegment(sketch, "E458.MirrorCS", {"start": v(-2355.85, -482.6) * mm, "end": v(-2241.55, -482.6) * mm});
            skLineSegment(sketch, "E459.MirrorCS", {"start": v(-2355.85, -464.31) * mm, "end": v(-2355.85, -482.6) * mm});
            skLineSegment(sketch, "E460.MirrorCS", {"start": v(-2241.55, -464.31) * mm, "end": v(-2241.55, -482.6) * mm});
            skPoint(sketch, "E461.MirrorP", {"position": v(-2298.7, -473.46) * mm});
            skLineSegment(sketch, "E462", {"start": v(-1930.4, -362.71) * mm, "end": v(-1879.6, -261.11) * mm});
            skLineSegment(sketch, "E463", {"start": v(-1879.6, -261.11) * mm, "end": v(-990.6, -210.31) * mm});
            skLineSegment(sketch, "E464.bottom", {"start": v(2895.6, -196.09) * mm, "end": v(2870.2, -196.09) * mm, "construction": true});
            skLineSegment(sketch, "E464.top", {"start": v(2895.6, -221.49) * mm, "end": v(2870.2, -221.49) * mm, "construction": true});
            skLineSegment(sketch, "E464.left", {"start": v(2895.6, -196.09) * mm, "end": v(2895.6, -221.49) * mm, "construction": true});
            skLineSegment(sketch, "E464.right", {"start": v(2870.2, -196.09) * mm, "end": v(2870.2, -221.49) * mm, "construction": true});
            skCircle(sketch, "E465", {"center": v(2870.2, -221.49) * mm, "radius": 5.59 * mm});
            skLineSegment(sketch, "E466", {"start": v(2895.6, -304.8) * mm, "end": v(2939.29, -304.8) * mm, "construction": true});
            skCircle(sketch, "E467.MirrorC", {"center": v(2870.2, -388.11) * mm, "radius": 5.59 * mm});
            skCircle(sketch, "E468.MirrorC", {"center": v(1143, -221.49) * mm, "radius": 5.59 * mm});
            skCircle(sketch, "E469.MirrorC", {"center": v(1143, -388.11) * mm, "radius": 5.59 * mm});
            skLineSegment(sketch, "E470.bottom", {"start": v(279.4, 2463.8) * mm, "end": v(355.6, 2463.8) * mm, "construction": true});
            skLineSegment(sketch, "E470.top", {"start": v(279.4, 2438.4) * mm, "end": v(355.6, 2438.4) * mm, "construction": true});
            skLineSegment(sketch, "E470.left", {"start": v(279.4, 2463.8) * mm, "end": v(279.4, 2438.4) * mm, "construction": true});
            skLineSegment(sketch, "E470.right", {"start": v(355.6, 2463.8) * mm, "end": v(355.6, 2438.4) * mm, "construction": true});
            skCircle(sketch, "E471", {"center": v(355.6, 2438.4) * mm, "radius": 5.59 * mm});
            skCircle(sketch, "E472.MirrorC", {"center": v(762, 2438.4) * mm, "radius": 5.59 * mm});
            skCircle(sketch, "E473.MirrorC", {"center": v(355.6, 711.2) * mm, "radius": 5.59 * mm});
            skCircle(sketch, "E474.MirrorC", {"center": v(762, 711.2) * mm, "radius": 5.59 * mm});
            skCircle(sketch, "E475", {"center": v(301.24, -299.21) * mm, "radius": 3.81 * mm});
            skPoint(sketch, "E475.centerSnap0", {"position": v(301.24, -261.11) * mm});
            skCircle(sketch, "E476.MirrorC", {"center": v(-301.24, -299.21) * mm, "radius": 3.81 * mm});
            skLineSegment(sketch, "E477.bottom", {"start": v(-990.6, -261.11) * mm, "end": v(-1016, -261.11) * mm, "construction": true});
            skLineSegment(sketch, "E477.top", {"start": v(-990.6, -299.21) * mm, "end": v(-1016, -299.21) * mm, "construction": true});
            skLineSegment(sketch, "E477.left", {"start": v(-990.6, -261.11) * mm, "end": v(-990.6, -299.21) * mm, "construction": true});
            skLineSegment(sketch, "E477.right", {"start": v(-1016, -261.11) * mm, "end": v(-1016, -299.21) * mm, "construction": true});
            skCircle(sketch, "E478", {"center": v(-1016, -299.21) * mm, "radius": 5.59 * mm});
            skCircle(sketch, "E479", {"center": v(-59.94, 1155.7) * mm, "radius": 5.59 * mm});
            skPoint(sketch, "E479.centerSnap0", {"position": v(-59.94, 1473.2) * mm});
            skPoint(sketch, "E479.centerSnap1", {"position": v(-292.1, 1155.7) * mm});
            skLineSegment(sketch, "E480.bottom", {"start": v(-1096.33, 2451.1) * mm, "end": v(-1138.54, 2451.1) * mm, "construction": true});
            skLineSegment(sketch, "E480.top", {"start": v(-1096.33, 2181.8) * mm, "end": v(-1138.54, 2181.8) * mm, "construction": true});
            skLineSegment(sketch, "E480.left", {"start": v(-1096.33, 2451.1) * mm, "end": v(-1096.33, 2181.8) * mm, "construction": true});
            skLineSegment(sketch, "E480.right", {"start": v(-1138.54, 2451.1) * mm, "end": v(-1138.54, 2181.8) * mm, "construction": true});
            skLineSegment(sketch, "E481.bottom", {"start": v(-1138.54, 2451.1) * mm, "end": v(-1163.94, 2451.1) * mm});
            skLineSegment(sketch, "E481.top", {"start": v(-1138.54, 2400.3) * mm, "end": v(-1163.94, 2400.3) * mm});
            skLineSegment(sketch, "E481.left", {"start": v(-1138.54, 2451.1) * mm, "end": v(-1138.54, 2400.3) * mm});
            skLineSegment(sketch, "E481.right", {"start": v(-1163.94, 2451.1) * mm, "end": v(-1163.94, 2400.3) * mm});
            skLineSegment(sketch, "E482.bottom", {"start": v(-1138.54, 2181.8) * mm, "end": v(-1163.94, 2181.8) * mm});
            skLineSegment(sketch, "E482.top", {"start": v(-1138.54, 2131) * mm, "end": v(-1163.94, 2131) * mm});
            skLineSegment(sketch, "E482.left", {"start": v(-1138.54, 2181.8) * mm, "end": v(-1138.54, 2131) * mm});
            skLineSegment(sketch, "E482.right", {"start": v(-1163.94, 2181.8) * mm, "end": v(-1163.94, 2131) * mm});
            skLineSegment(sketch, "E483.bottom", {"start": v(-1138.54, 2131) * mm, "end": v(-1120.25, 2131) * mm});
            skLineSegment(sketch, "E483.top", {"start": v(-1138.54, 2451.1) * mm, "end": v(-1120.25, 2451.1) * mm});
            skLineSegment(sketch, "E483.left", {"start": v(-1138.54, 2131) * mm, "end": v(-1138.54, 2451.1) * mm});
            skLineSegment(sketch, "E483.right", {"start": v(-1120.25, 2131) * mm, "end": v(-1120.25, 2451.1) * mm});
            skLineSegment(sketch, "E484.bottom", {"start": v(-1163.94, 2451.1) * mm, "end": v(-1011.54, 2451.1) * mm});
            skLineSegment(sketch, "E484.top", {"start": v(-1163.94, 2482.09) * mm, "end": v(-1011.54, 2482.09) * mm});
            skLineSegment(sketch, "E484.left", {"start": v(-1163.94, 2451.1) * mm, "end": v(-1163.94, 2482.09) * mm});
            skLineSegment(sketch, "E484.right", {"start": v(-1011.54, 2451.1) * mm, "end": v(-1011.54, 2482.09) * mm});
            skSolve(sketch);
        }
        {
            var Q0;
            {var subQ25=sQuery(id+"F1.wireOp",EDGE,"E45.bottom");Q0=makeQuery(id+"F1.imprint","IMPRINT",FACE,{"disambiguationData":[TD([[makeQuery(id+"F1.imprint","IMPRINT",EDGE,{"derivedFrom":subQ25}),1.0]])]});}
            var Q1;
            Q1=makeQuery(id+"F1.imprint","IMPRINT",FACE,{"disambiguationData":[TD([[makeQuery(id+"F1.imprint","IMPRINT",EDGE,{"derivedFrom":sQuery(id+"F1.wireOp",EDGE,"E52.MirrorCS")}),-1.0]])]});
            var Q2;
            Q2=makeQuery(id+"F1.imprint","IMPRINT",FACE,{"disambiguationData":[TD([[makeQuery(id+"F1.imprint","IMPRINT",EDGE,{"derivedFrom":sQuery(id+"F1.wireOp",EDGE,"E56.MirrorCS")}),-1.0]])]});
            var Q3;
            Q3=makeQuery(id+"F1.imprint","IMPRINT",FACE,{"disambiguationData":[TD([[makeQuery(id+"F1.imprint","IMPRINT",EDGE,{"derivedFrom":sQuery(id+"F1.wireOp",EDGE,"E48.MirrorCS")}),-1.0]])]});
            var Q4;
            Q4=makeQuery(id+"F1.imprint","IMPRINT",FACE,{"disambiguationData":[TD([[makeQuery(id+"F1.imprint","IMPRINT",EDGE,{"derivedFrom":sQuery(id+"F1.wireOp",EDGE,"E45.bottom")}),-1.0]])]});
            var Q5;
            Q5=makeQuery(id+"F1.imprint","IMPRINT",FACE,{"disambiguationData":[TD([[makeQuery(id+"F1.imprint","IMPRINT",EDGE,{"derivedFrom":sQuery(id+"F1.wireOp",EDGE,"E63.bottom")}),1.0]])]});
            var Q6;
            Q6=makeQuery(id+"F1.imprint","IMPRINT",FACE,{"disambiguationData":[TD([[makeQuery(id+"F1.imprint","IMPRINT",EDGE,{"derivedFrom":sQuery(id+"F1.wireOp",EDGE,"E64.bottom")}),-1.0]])]});
            var Q7;
            Q7=makeQuery(id+"F1.imprint","IMPRINT",FACE,{"disambiguationData":[TD([[makeQuery(id+"F1.imprint","IMPRINT",EDGE,{"derivedFrom":sQuery(id+"F1.wireOp",EDGE,"E67.MirrorCS")}),1.0]])]});
            var Q8;
            Q8=makeQuery(id+"F1.imprint","IMPRINT",FACE,{"disambiguationData":[TD([[makeQuery(id+"F1.imprint","IMPRINT",EDGE,{"derivedFrom":sQuery(id+"F1.wireOp",EDGE,"E307.bottom")}),-1.0]])]});
            var Q9;
            Q9=makeQuery(id+"F1.imprint","IMPRINT",FACE,{"disambiguationData":[TD([[makeQuery(id+"F1.imprint","IMPRINT",EDGE,{"derivedFrom":sQuery(id+"F1.wireOp",EDGE,"E308.MirrorCS")}),-1.0]])]});
            var Q10;
            Q10=makeQuery(id+"F1.imprint","IMPRINT",FACE,{"disambiguationData":[TD([[makeQuery(id+"F1.imprint","IMPRINT",EDGE,{"derivedFrom":sQuery(id+"F1.wireOp",EDGE,"E343.top")}),1.0]])]});
            var Q11;
            Q11=makeQuery(id+"F1.imprint","IMPRINT",FACE,{"disambiguationData":[TD([[makeQuery(id+"F1.imprint","IMPRINT",EDGE,{"derivedFrom":sQuery(id+"F1.wireOp",EDGE,"E342.bottom")}),1.0]])]});
            var Q12;
            Q12=makeQuery(id+"F1.imprint","IMPRINT",FACE,{"disambiguationData":[TD([[makeQuery(id+"F1.imprint","IMPRINT",EDGE,{"derivedFrom":sQuery(id+"F1.wireOp",EDGE,"E75.MirrorCS")}),-1.0]])]});
            var Q13;
            Q13=makeQuery(id+"F1.imprint","IMPRINT",FACE,{"disambiguationData":[TD([[makeQuery(id+"F1.imprint","IMPRINT",EDGE,{"derivedFrom":sQuery(id+"F1.wireOp",EDGE,"E71.MirrorCS")}),1.0]])]});
            var Q14;
            {var subQ14=sQuery(id+"F1.wireOp",EDGE,"E0.left");Q14=makeQuery(id+"F1.imprint","IMPRINT",FACE,{"disambiguationData":[TD([[makeQuery(id+"F1.imprint","IMPRINT",EDGE,{"derivedFrom":subQ14}),-1.0]])]});}
            var Q15;
            {var subQ8=sQuery(id+"F1.wireOp",EDGE,"E87");Q15=makeQuery(id+"F1.imprint","IMPRINT",FACE,{"disambiguationData":[TD([[makeQuery(id+"F1.imprint","IMPRINT",EDGE,{"derivedFrom":subQ8}),-1.0]])]});}
            var Q16;
            Q16=makeQuery(id+"F1.imprint","IMPRINT",FACE,{"disambiguationData":[TD([[makeQuery(id+"F1.imprint","IMPRINT",EDGE,{"derivedFrom":sQuery(id+"F1.wireOp",EDGE,"E208.MirrorCS")}),-1.0]])]});
            var Q17;
            Q17=makeQuery(id+"F1.imprint","IMPRINT",FACE,{"disambiguationData":[TD([[makeQuery(id+"F1.imprint","IMPRINT",EDGE,{"derivedFrom":sQuery(id+"F1.wireOp",EDGE,"E110.bottom")}),1.0]])]});
            var Q18;
            Q18=makeQuery(id+"F1.imprint","IMPRINT",FACE,{"disambiguationData":[TD([[makeQuery(id+"F1.imprint","IMPRINT",EDGE,{"derivedFrom":sQuery(id+"F1.wireOp",EDGE,"E111.bottom")}),-1.0]])]});
            var Q19;
            Q19=makeQuery(id+"F1.imprint","IMPRINT",FACE,{"disambiguationData":[TD([[makeQuery(id+"F1.imprint","IMPRINT",EDGE,{"derivedFrom":sQuery(id+"F1.wireOp",EDGE,"E254.bottom")}),1.0]])]});
            var Q20;
            Q20=makeQuery(id+"F1.imprint","IMPRINT",FACE,{"disambiguationData":[TD([[makeQuery(id+"F1.imprint","IMPRINT",EDGE,{"derivedFrom":sQuery(id+"F1.wireOp",EDGE,"E253.bottom")}),-1.0]])]});
            var Q21;
            Q21=makeQuery(id+"F1.imprint","IMPRINT",FACE,{"disambiguationData":[TD([[makeQuery(id+"F1.imprint","IMPRINT",EDGE,{"derivedFrom":sQuery(id+"F1.wireOp",EDGE,"E99.top")}),-1.0]])]});
            var Q22;
            Q22=makeQuery(id+"F1.imprint","IMPRINT",FACE,{"disambiguationData":[TD([[makeQuery(id+"F1.imprint","IMPRINT",EDGE,{"derivedFrom":sQuery(id+"F1.wireOp",EDGE,"E255.MirrorCS")}),1.0]])]});
            var Q23;
            {var subQ0=sQuery(id+"F1.wireOp",EDGE,"E191.bottom");Q23=makeQuery(id+"F1.imprint","IMPRINT",FACE,{"disambiguationData":[TD([[makeQuery(id+"F1.imprint","IMPRINT",EDGE,{"derivedFrom":subQ0}),-1.0]])]});}
            var Q24;
            {var subQ0=sQuery(id+"F1.wireOp",EDGE,"E340.bottom");Q24=makeQuery(id+"F1.imprint","IMPRINT",FACE,{"disambiguationData":[TD([[makeQuery(id+"F1.imprint","IMPRINT",EDGE,{"derivedFrom":subQ0}),-1.0]])]});}
            var Q25;
            {var subQ3=sQuery(id+"F1.wireOp",EDGE,"E341.bottom");Q25=makeQuery(id+"F1.imprint","IMPRINT",FACE,{"disambiguationData":[TD([[makeQuery(id+"F1.imprint","IMPRINT",EDGE,{"derivedFrom":subQ3}),1.0]])]});}
            var Q26;
            {var subQ0=sQuery(id+"F1.wireOp",EDGE,"E151");Q26=makeQuery(id+"F1.imprint","IMPRINT",FACE,{"disambiguationData":[TD([[makeQuery(id+"F1.imprint","IMPRINT",EDGE,{"derivedFrom":subQ0}),1.0]])]});}
            var Q27;
            {var subQ1=sQuery(id+"F1.wireOp",EDGE,"E90");Q27=makeQuery(id+"F1.imprint","IMPRINT",FACE,{"disambiguationData":[TD([[makeQuery(id+"F1.imprint","IMPRINT",EDGE,{"derivedFrom":subQ1}),-1.0]])]});}
            var Q28;
            Q28=makeQuery(id+"F1.imprint","IMPRINT",FACE,{"disambiguationData":[TD([[makeQuery(id+"F1.imprint","IMPRINT",EDGE,{"derivedFrom":sQuery(id+"F1.wireOp",EDGE,"E94.bottom")}),1.0]])]});
            var Q29;
            Q29=makeQuery(id+"F1.imprint","IMPRINT",FACE,{"disambiguationData":[TD([[makeQuery(id+"F1.imprint","IMPRINT",EDGE,{"derivedFrom":sQuery(id+"F1.wireOp",EDGE,"E204.MirrorCS")}),1.0]])]});
            var Q30;
            Q30=makeQuery(id+"F1.imprint","IMPRINT",FACE,{"disambiguationData":[TD([[makeQuery(id+"F1.imprint","IMPRINT",EDGE,{"derivedFrom":sQuery(id+"F1.wireOp",EDGE,"E93.bottom")}),-1.0]])]});
            var Q31;
            Q31=makeQuery(id+"F1.imprint","IMPRINT",FACE,{"disambiguationData":[TD([[makeQuery(id+"F1.imprint","IMPRINT",EDGE,{"derivedFrom":sQuery(id+"F1.wireOp",EDGE,"E189.bottom")}),-1.0]])]});
            var Q32;
            {var subQ1=sQuery(id+"F1.wireOp",EDGE,"E179.MirrorCS");Q32=makeQuery(id+"F1.imprint","IMPRINT",FACE,{"disambiguationData":[TD([[makeQuery(id+"F1.imprint","IMPRINT",EDGE,{"derivedFrom":subQ1}),-1.0]])]});}
            var Q33;
            Q33=makeQuery(id+"F1.imprint","IMPRINT",FACE,{"disambiguationData":[TD([[makeQuery(id+"F1.imprint","IMPRINT",EDGE,{"derivedFrom":sQuery(id+"F1.wireOp",EDGE,"E174.MirrorCS")}),-1.0]])]});
            var Q34;
            Q34=makeQuery(id+"F1.imprint","IMPRINT",FACE,{"disambiguationData":[TD([[makeQuery(id+"F1.imprint","IMPRINT",EDGE,{"derivedFrom":sQuery(id+"F1.wireOp",EDGE,"E188.bottom")}),-1.0]])]});
            var Q35;
            Q35=makeQuery(id+"F1.imprint","IMPRINT",FACE,{"disambiguationData":[TD([[makeQuery(id+"F1.imprint","IMPRINT",EDGE,{"derivedFrom":sQuery(id+"F1.wireOp",EDGE,"E457.MirrorCS")}),-1.0]])]});
            var Q36;
            Q36=makeQuery(id+"F1.imprint","IMPRINT",FACE,{"disambiguationData":[TD([[makeQuery(id+"F1.imprint","IMPRINT",EDGE,{"derivedFrom":sQuery(id+"F1.wireOp",EDGE,"E449")}),-1.0]])]});
            var Q37;
            Q37=makeQuery(id+"F1.imprint","IMPRINT",FACE,{"disambiguationData":[TD([[makeQuery(id+"F1.imprint","IMPRINT",EDGE,{"derivedFrom":sQuery(id+"F1.wireOp",EDGE,"E455.bottom")}),1.0]])]});
            var Q38;
            Q38=makeQuery(id+"F1.imprint","IMPRINT",FACE,{"disambiguationData":[TD([[makeQuery(id+"F1.imprint","IMPRINT",EDGE,{"derivedFrom":sQuery(id+"F1.wireOp",EDGE,"E454.bottom")}),1.0]])]});
            var Q39;
            Q39=makeQuery(id+"F1.imprint","IMPRINT",FACE,{"disambiguationData":[TD([[makeQuery(id+"F1.imprint","IMPRINT",EDGE,{"derivedFrom":sQuery(id+"F1.wireOp",EDGE,"E453.bottom")}),-1.0]])]});
            extrude(context, id + "F2", {"entities" : qUnion([Q0, Q1, Q2, Q3, Q4, Q5, Q6, Q7, Q8, Q9, Q10, Q11, Q12, Q13, Q14, Q15, Q16, Q17, Q18, Q19, Q20, Q21, Q22, Q23, Q24, Q25, Q26, Q27, Q28, Q29, Q30, Q31, Q32, Q33, Q34, Q35, Q36, Q37, Q38, Q39]), "depth" : (getVariable(context, 'ply34')) * mm});
        }
    });
